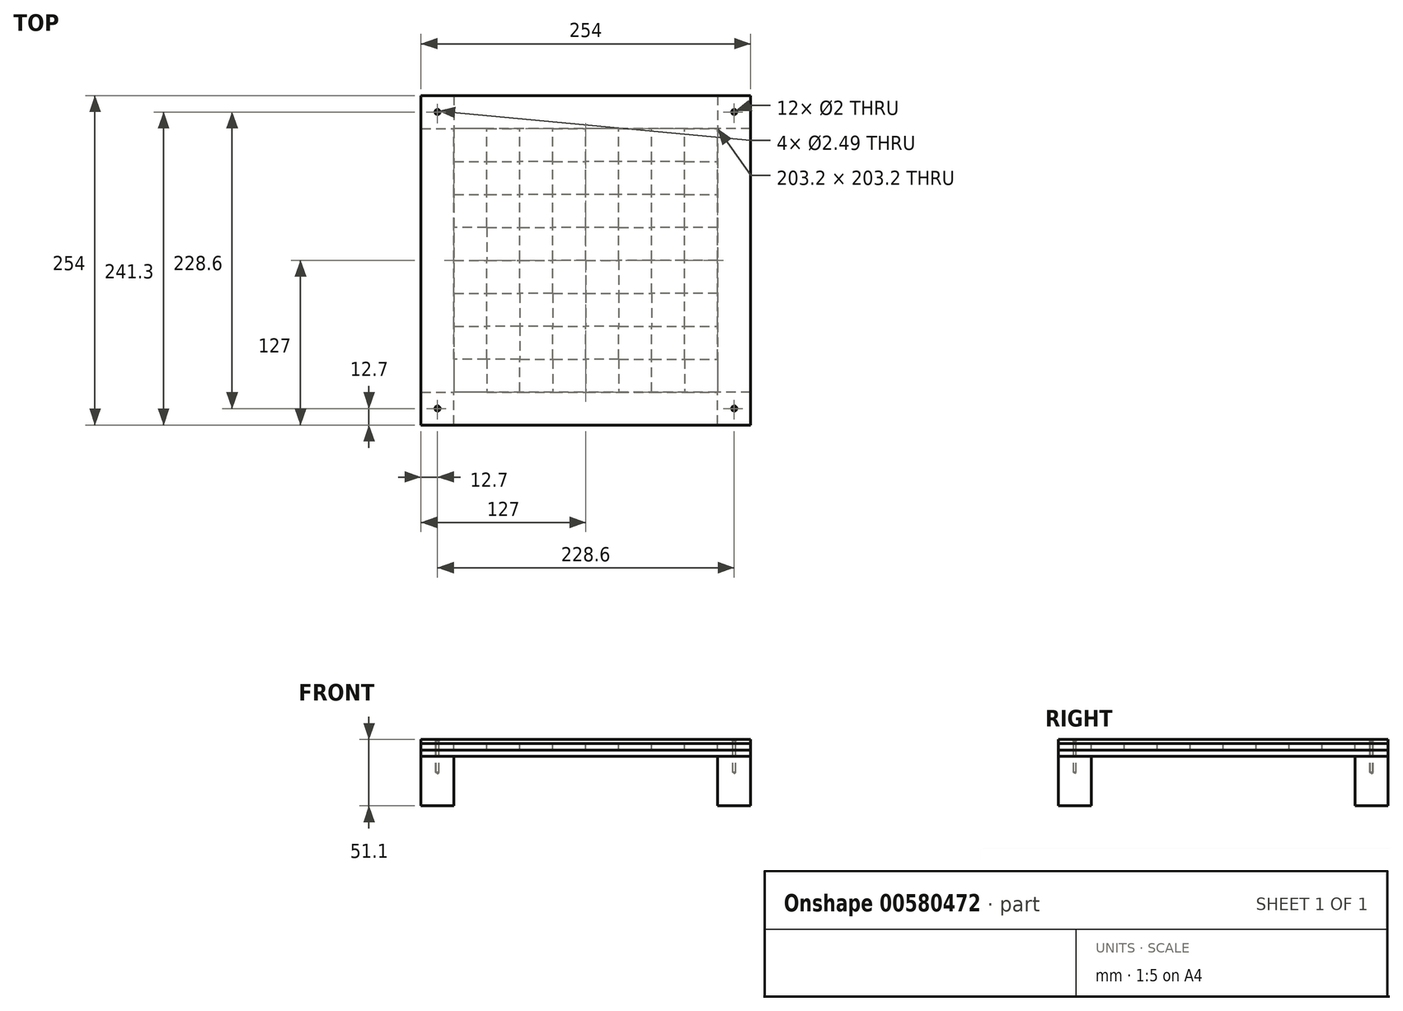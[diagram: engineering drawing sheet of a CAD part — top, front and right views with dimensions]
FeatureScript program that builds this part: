
annotation { "Feature Type Name" : "Feature", "Feature Type Description" : "" }
export const myFeature = defineFeature(function(context is Context, id is Id, definition is map)
    precondition{}
    {
        {
            var Q0;
            Q0=qCreatedBy(makeId("Top.planeOp"),FACE);
            var sketch = newSketch(context, id + "F0", { "sketchPlane" : qUnion([Q0])});
            skLineSegment(sketch, "E0.bottom", {"start": v(127, 127) * mm, "end": v(-127, 127) * mm});
            skLineSegment(sketch, "E0.top", {"start": v(127, -127) * mm, "end": v(-127, -127) * mm});
            skLineSegment(sketch, "E0.left", {"start": v(127, 127) * mm, "end": v(127, -127) * mm});
            skLineSegment(sketch, "E0.right", {"start": v(-127, 127) * mm, "end": v(-127, -127) * mm});
            skPoint(sketch, "E0.middle", {"position": v(0, 0) * mm});
            skSolve(sketch);
        }
        {
            var Q0;
            Q0=qCreatedBy(makeId("Top.planeOp"),FACE);
            var sketch = newSketch(context, id + "F1", { "sketchPlane" : qUnion([Q0])});
            skLineSegment(sketch, "E1.bottom", {"start": v(-127, 127) * mm, "end": v(127, 127) * mm});
            skLineSegment(sketch, "E1.top", {"start": v(-127, -127) * mm, "end": v(127, -127) * mm});
            skLineSegment(sketch, "E1.left", {"start": v(-127, 127) * mm, "end": v(-127, -127) * mm});
            skLineSegment(sketch, "E1.right", {"start": v(127, 127) * mm, "end": v(127, -127) * mm});
            skPoint(sketch, "E1.middle", {"position": v(0, 0) * mm});
            skSolve(sketch);
        }
        {
            var Q0;
            Q0 = qSketchRegion(id + "F1", true);
            extrude(context, id + "F2", {"entities" : qUnion([Q0]), "oppositeDirection" : true, "depth" : 5 * mm, "offsetDistance" : 25.4 * mm});
        }
        {
            var Q0;
            Q0 = qSketchRegion(id + "F0", true);
            extrude(context, id + "F3", {"entities" : qUnion([Q0]), "depth" : 3 * mm, "offsetDistance" : 25.4 * mm});
        }
        {
            var Q0;
            Q0=makeQuery(id+"F2.opExtrude","CAP_FACE",FACE,{"disambiguationData":[OSD([sQuery(id+"F1.wireOp",EDGE,"E1.bottom"),sQuery(id+"F1.wireOp",EDGE,"E1.top"),sQuery(id+"F1.wireOp",EDGE,"E1.left"),sQuery(id+"F1.wireOp",EDGE,"E1.right")])],"isStart":false});
            extrude(context, id + "F4", {"entities" : qUnion([Q0]), "depth" : 5 * mm, "offsetDistance" : 25.4 * mm});
        }
        {
            var Q0;
            Q0=makeQuery(id+"F4.opExtrude","CAP_FACE",FACE,{"disambiguationData":[OSD([sQuery(id+"F1.wireOp",EDGE,"E1.bottom"),sQuery(id+"F1.wireOp",EDGE,"E1.top"),sQuery(id+"F1.wireOp",EDGE,"E1.left"),sQuery(id+"F1.wireOp",EDGE,"E1.right")])],"isStart":false});
            var sketch = newSketch(context, id + "F5", { "sketchPlane" : qUnion([Q0])});
            skLineSegment(sketch, "E2.bottom", {"start": v(-127, 127) * mm, "end": v(-101.6, 127) * mm});
            skLineSegment(sketch, "E2.top", {"start": v(-127, 101.6) * mm, "end": v(-101.6, 101.6) * mm});
            skLineSegment(sketch, "E2.left", {"start": v(-127, 127) * mm, "end": v(-127, 101.6) * mm});
            skLineSegment(sketch, "E2.right", {"start": v(-101.6, 127) * mm, "end": v(-101.6, 101.6) * mm});
            skSolve(sketch);
        }
        {
            var Q0;
            Q0 = qSketchRegion(id + "F5", true);
            extrude(context, id + "F6", {"entities" : qUnion([Q0]), "depth" : 38.1 * mm, "offsetDistance" : 25.4 * mm});
        }
        {
            var Q0;
            Q0=makeQuery(id+"F4.opExtrude","CAP_FACE",FACE,{"disambiguationData":[OSD([sQuery(id+"F1.wireOp",EDGE,"E1.bottom"),sQuery(id+"F1.wireOp",EDGE,"E1.top"),sQuery(id+"F1.wireOp",EDGE,"E1.left"),sQuery(id+"F1.wireOp",EDGE,"E1.right")])],"isStart":false});
            var sketch = newSketch(context, id + "F7", { "sketchPlane" : qUnion([Q0])});
            skLineSegment(sketch, "E3.bottom", {"start": v(127, 127) * mm, "end": v(101.6, 127) * mm});
            skLineSegment(sketch, "E3.top", {"start": v(127, 101.6) * mm, "end": v(101.6, 101.6) * mm});
            skLineSegment(sketch, "E3.left", {"start": v(127, 127) * mm, "end": v(127, 101.6) * mm});
            skLineSegment(sketch, "E3.right", {"start": v(101.6, 127) * mm, "end": v(101.6, 101.6) * mm});
            skSolve(sketch);
        }
        {
            var Q0;
            Q0=makeQuery(id+"F7.imprint","IMPRINT",FACE,{"disambiguationData":[TD([[makeQuery(id+"F7.imprint","IMPRINT",EDGE,{"derivedFrom":sQuery(id+"F7.wireOp",EDGE,"E3.bottom")}),-1.0]])]});
            extrude(context, id + "F8", {"entities" : qUnion([Q0]), "depth" : 38.1 * mm, "offsetDistance" : 25.4 * mm});
        }
        {
            var Q0;
            Q0=makeQuery(id+"F4.opExtrude","CAP_FACE",FACE,{"disambiguationData":[OSD([sQuery(id+"F1.wireOp",EDGE,"E1.bottom"),sQuery(id+"F1.wireOp",EDGE,"E1.top"),sQuery(id+"F1.wireOp",EDGE,"E1.left"),sQuery(id+"F1.wireOp",EDGE,"E1.right")])],"isStart":false});
            var sketch = newSketch(context, id + "F9", { "sketchPlane" : qUnion([Q0])});
            skLineSegment(sketch, "E4.bottom", {"start": v(127, -127) * mm, "end": v(101.6, -127) * mm});
            skLineSegment(sketch, "E4.top", {"start": v(127, -101.6) * mm, "end": v(101.6, -101.6) * mm});
            skLineSegment(sketch, "E4.left", {"start": v(127, -127) * mm, "end": v(127, -101.6) * mm});
            skLineSegment(sketch, "E4.right", {"start": v(101.6, -127) * mm, "end": v(101.6, -101.6) * mm});
            skSolve(sketch);
        }
        {
            var Q0;
            Q0 = qSketchRegion(id + "F9", true);
            extrude(context, id + "F10", {"entities" : qUnion([Q0]), "depth" : 38.1 * mm, "offsetDistance" : 25.4 * mm});
        }
        {
            var Q0;
            Q0=makeQuery(id+"F4.opExtrude","CAP_FACE",FACE,{"disambiguationData":[OSD([sQuery(id+"F1.wireOp",EDGE,"E1.bottom"),sQuery(id+"F1.wireOp",EDGE,"E1.top"),sQuery(id+"F1.wireOp",EDGE,"E1.left"),sQuery(id+"F1.wireOp",EDGE,"E1.right")])],"isStart":false});
            var sketch = newSketch(context, id + "F11", { "sketchPlane" : qUnion([Q0])});
            skLineSegment(sketch, "E5.bottom", {"start": v(-127, -127) * mm, "end": v(-101.6, -127) * mm});
            skLineSegment(sketch, "E5.top", {"start": v(-127, -101.6) * mm, "end": v(-101.6, -101.6) * mm});
            skLineSegment(sketch, "E5.left", {"start": v(-127, -127) * mm, "end": v(-127, -101.6) * mm});
            skLineSegment(sketch, "E5.right", {"start": v(-101.6, -127) * mm, "end": v(-101.6, -101.6) * mm});
            skSolve(sketch);
        }
        {
            var Q0;
            Q0=makeQuery(id+"F11.imprint","IMPRINT",FACE,{"disambiguationData":[TD([[makeQuery(id+"F11.imprint","IMPRINT",EDGE,{"derivedFrom":sQuery(id+"F11.wireOp",EDGE,"E5.bottom")}),1.0]])]});
            extrude(context, id + "F12", {"entities" : qUnion([Q0]), "depth" : 38.1 * mm, "offsetDistance" : 25.4 * mm});
        }
        {
            var Q0;
            Q0=makeQuery(id+"F3.opExtrude","CAP_FACE",FACE,{"disambiguationData":[OSD([sQuery(id+"F0.wireOp",EDGE,"E0.bottom"),sQuery(id+"F0.wireOp",EDGE,"E0.top"),sQuery(id+"F0.wireOp",EDGE,"E0.left"),sQuery(id+"F0.wireOp",EDGE,"E0.right")])],"isStart":false});
            var sketch = newSketch(context, id + "F13", { "sketchPlane" : qUnion([Q0])});
            skCircle(sketch, "E6", {"center": v(-114.3, 114.3) * mm, "radius": 3.81 * mm});
            skSolve(sketch);
        }
        {
            var Q0;
            Q0=sQuery(id+"F13.wireOp",VERTEX,"E6.center");
            var Q1;
            Q1=makeQuery(id+"F2.opExtrude","SWEPT_BODY",BODY,{"disambiguationData":[OSD([sQuery(id+"F1.wireOp",EDGE,"E1.bottom"),sQuery(id+"F1.wireOp",EDGE,"E1.top"),sQuery(id+"F1.wireOp",EDGE,"E1.left"),sQuery(id+"F1.wireOp",EDGE,"E1.right")])]});
            var Q2;
            Q2=makeQuery(id+"F3.opExtrude","SWEPT_BODY",BODY,{"disambiguationData":[OSD([sQuery(id+"F0.wireOp",EDGE,"E0.bottom"),sQuery(id+"F0.wireOp",EDGE,"E0.top"),sQuery(id+"F0.wireOp",EDGE,"E0.left"),sQuery(id+"F0.wireOp",EDGE,"E0.right")])]});
            var Q3;
            Q3=makeQuery(id+"F4.opExtrude","SWEPT_BODY",BODY,{"disambiguationData":[OSD([sQuery(id+"F1.wireOp",EDGE,"E1.bottom"),sQuery(id+"F1.wireOp",EDGE,"E1.top"),sQuery(id+"F1.wireOp",EDGE,"E1.left"),sQuery(id+"F1.wireOp",EDGE,"E1.right")])]});
            var Q4;
            Q4=makeQuery(id+"F12.opExtrude","SWEPT_BODY",BODY,{"disambiguationData":[OSD([sQuery(id+"F11.wireOp",EDGE,"E5.bottom"),sQuery(id+"F11.wireOp",EDGE,"E5.top"),sQuery(id+"F11.wireOp",EDGE,"E5.left"),sQuery(id+"F11.wireOp",EDGE,"E5.right")])]});
            hole(context, id + "F14", {"style" : HoleStyle.SIMPLE, "endStyle" : HoleEndStyle.BLIND, "holeDiameter" : 2.5 * mm, "holeDepth" : 25.4 * mm, "isTappedThrough" : true, "tappedDepth" : 12.7 * mm, "tapClearance" : 3, "locations" : qUnion([Q0]), "scope" : qUnion([Q1, Q2, Q3, Q4])});
        }
        {
            var Q0;
            Q0=makeQuery(id+"F3.opExtrude","CAP_FACE",FACE,{"disambiguationData":[OSD([sQuery(id+"F0.wireOp",EDGE,"E0.bottom"),sQuery(id+"F0.wireOp",EDGE,"E0.top"),sQuery(id+"F0.wireOp",EDGE,"E0.left"),sQuery(id+"F0.wireOp",EDGE,"E0.right")])],"isStart":false});
            var sketch = newSketch(context, id + "F15", { "sketchPlane" : qUnion([Q0])});
            skPoint(sketch, "E7", {"position": v(-114.3, 114.3) * mm});
            skCircle(sketch, "E8", {"center": v(-114.3, 114.3) * mm, "radius": 2 * mm});
            skSolve(sketch);
        }
        {
            var Q0;
            Q0=sQuery(id+"F15.wireOp",VERTEX,"E7");
            var Q1;
            Q1=makeQuery(id+"F3.opExtrude","SWEPT_BODY",BODY,{"disambiguationData":[OSD([sQuery(id+"F0.wireOp",EDGE,"E0.bottom"),sQuery(id+"F0.wireOp",EDGE,"E0.top"),sQuery(id+"F0.wireOp",EDGE,"E0.left"),sQuery(id+"F0.wireOp",EDGE,"E0.right")])]});
            hole(context, id + "F16", {"style" : HoleStyle.C_SINK, "endStyle" : HoleEndStyle.BLIND, "holeDiameter" : 2.5 * mm, "cSinkDiameter" : 4 * mm, "cSinkAngle" : 90 * degree, "holeDepth" : 4 * mm, "isTappedThrough" : true, "tappedDepth" : 12.7 * mm, "tapClearance" : 3, "locations" : qUnion([Q0]), "scope" : qUnion([Q1])});
        }
        {
            var Q0;
            Q0=makeQuery(id+"F3.opExtrude","CAP_FACE",FACE,{"disambiguationData":[OSD([sQuery(id+"F0.wireOp",EDGE,"E0.bottom"),sQuery(id+"F0.wireOp",EDGE,"E0.top"),sQuery(id+"F0.wireOp",EDGE,"E0.left"),sQuery(id+"F0.wireOp",EDGE,"E0.right")])],"isStart":false});
            var sketch = newSketch(context, id + "F17", { "sketchPlane" : qUnion([Q0])});
            skCircle(sketch, "E9", {"center": v(114.3, 114.3) * mm, "radius": 2 * mm});
            skSolve(sketch);
        }
        {
            var Q0;
            Q0=sQuery(id+"F17.wireOp",VERTEX,"E9.center");
            var Q1;
            Q1=makeQuery(id+"F2.opExtrude","SWEPT_BODY",BODY,{"disambiguationData":[OSD([sQuery(id+"F1.wireOp",EDGE,"E1.bottom"),sQuery(id+"F1.wireOp",EDGE,"E1.top"),sQuery(id+"F1.wireOp",EDGE,"E1.left"),sQuery(id+"F1.wireOp",EDGE,"E1.right")])]});
            var Q2;
            Q2=makeQuery(id+"F3.opExtrude","SWEPT_BODY",BODY,{"disambiguationData":[OSD([sQuery(id+"F0.wireOp",EDGE,"E0.bottom"),sQuery(id+"F0.wireOp",EDGE,"E0.top"),sQuery(id+"F0.wireOp",EDGE,"E0.left"),sQuery(id+"F0.wireOp",EDGE,"E0.right")])]});
            var Q3;
            Q3=makeQuery(id+"F4.opExtrude","SWEPT_BODY",BODY,{"disambiguationData":[OSD([sQuery(id+"F1.wireOp",EDGE,"E1.bottom"),sQuery(id+"F1.wireOp",EDGE,"E1.top"),sQuery(id+"F1.wireOp",EDGE,"E1.left"),sQuery(id+"F1.wireOp",EDGE,"E1.right")])]});
            var Q4;
            Q4=makeQuery(id+"F10.opExtrude","SWEPT_BODY",BODY,{"disambiguationData":[OSD([sQuery(id+"F9.wireOp",EDGE,"E4.bottom"),sQuery(id+"F9.wireOp",EDGE,"E4.top"),sQuery(id+"F9.wireOp",EDGE,"E4.left"),sQuery(id+"F9.wireOp",EDGE,"E4.right")])]});
            hole(context, id + "F18", {"style" : HoleStyle.SIMPLE, "endStyle" : HoleEndStyle.BLIND, "holeDiameter" : 2 * mm, "holeDepth" : 25.4 * mm, "isTappedThrough" : true, "tappedDepth" : 12.7 * mm, "tapClearance" : 3, "locations" : qUnion([Q0]), "scope" : qUnion([Q1, Q2, Q3, Q4])});
        }
        {
            var Q0;
            Q0=makeQuery(id+"F3.opExtrude","CAP_FACE",FACE,{"disambiguationData":[OSD([sQuery(id+"F0.wireOp",EDGE,"E0.bottom"),sQuery(id+"F0.wireOp",EDGE,"E0.top"),sQuery(id+"F0.wireOp",EDGE,"E0.left"),sQuery(id+"F0.wireOp",EDGE,"E0.right")])],"isStart":false});
            var sketch = newSketch(context, id + "F19", { "sketchPlane" : qUnion([Q0])});
            skPoint(sketch, "E10", {"position": v(114.3, 114.3) * mm});
            skSolve(sketch);
        }
        {
            var Q0;
            Q0=sQuery(id+"F19.wireOp",VERTEX,"E10");
            var Q1;
            Q1=makeQuery(id+"F3.opExtrude","SWEPT_BODY",BODY,{"disambiguationData":[OSD([sQuery(id+"F0.wireOp",EDGE,"E0.bottom"),sQuery(id+"F0.wireOp",EDGE,"E0.top"),sQuery(id+"F0.wireOp",EDGE,"E0.left"),sQuery(id+"F0.wireOp",EDGE,"E0.right")])]});
            hole(context, id + "F20", {"style" : HoleStyle.C_SINK, "endStyle" : HoleEndStyle.BLIND, "holeDiameter" : 2 * mm, "cSinkDiameter" : 4 * mm, "cSinkAngle" : 90 * degree, "holeDepth" : 4 * mm, "isTappedThrough" : true, "tappedDepth" : 12.7 * mm, "tapClearance" : 3, "startFromSketch" : true, "locations" : qUnion([Q0]), "scope" : qUnion([Q1])});
        }
        {
            var Q0;
            Q0=makeQuery(id+"F3.opExtrude","CAP_FACE",FACE,{"disambiguationData":[OSD([sQuery(id+"F0.wireOp",EDGE,"E0.bottom"),sQuery(id+"F0.wireOp",EDGE,"E0.top"),sQuery(id+"F0.wireOp",EDGE,"E0.left"),sQuery(id+"F0.wireOp",EDGE,"E0.right")])],"isStart":false});
            var sketch = newSketch(context, id + "F21", { "sketchPlane" : qUnion([Q0])});
            skCircle(sketch, "E11", {"center": v(114.3, -114.3) * mm, "radius": 1 * mm});
            skCircle(sketch, "E12", {"center": v(-114.3, -114.3) * mm, "radius": 1 * mm});
            skSolve(sketch);
        }
        {
            var Q0;
            Q0=sQuery(id+"F21.wireOp",VERTEX,"E12.center");
            var Q1;
            Q1=makeQuery(id+"F2.opExtrude","SWEPT_BODY",BODY,{"disambiguationData":[OSD([sQuery(id+"F1.wireOp",EDGE,"E1.bottom"),sQuery(id+"F1.wireOp",EDGE,"E1.top"),sQuery(id+"F1.wireOp",EDGE,"E1.left"),sQuery(id+"F1.wireOp",EDGE,"E1.right")])]});
            var Q2;
            Q2=makeQuery(id+"F3.opExtrude","SWEPT_BODY",BODY,{"disambiguationData":[OSD([sQuery(id+"F0.wireOp",EDGE,"E0.bottom"),sQuery(id+"F0.wireOp",EDGE,"E0.top"),sQuery(id+"F0.wireOp",EDGE,"E0.left"),sQuery(id+"F0.wireOp",EDGE,"E0.right")])]});
            var Q3;
            Q3=makeQuery(id+"F4.opExtrude","SWEPT_BODY",BODY,{"disambiguationData":[OSD([sQuery(id+"F1.wireOp",EDGE,"E1.bottom"),sQuery(id+"F1.wireOp",EDGE,"E1.top"),sQuery(id+"F1.wireOp",EDGE,"E1.left"),sQuery(id+"F1.wireOp",EDGE,"E1.right")])]});
            var Q4;
            Q4=makeQuery(id+"F6.opExtrude","SWEPT_BODY",BODY,{"disambiguationData":[OSD([sQuery(id+"F5.wireOp",EDGE,"E2.bottom"),sQuery(id+"F5.wireOp",EDGE,"E2.top"),sQuery(id+"F5.wireOp",EDGE,"E2.left"),sQuery(id+"F5.wireOp",EDGE,"E2.right")])]});
            hole(context, id + "F22", {"style" : HoleStyle.SIMPLE, "endStyle" : HoleEndStyle.BLIND, "holeDiameter" : 2 * mm, "holeDepth" : 25.4 * mm, "isTappedThrough" : true, "tappedDepth" : 12 * mm, "tapClearance" : 3, "locations" : qUnion([Q0]), "scope" : qUnion([Q1, Q2, Q3, Q4])});
        }
        {
            var Q0;
            Q0=sQuery(id+"F21.wireOp",VERTEX,"E11.center");
            var Q1;
            Q1=makeQuery(id+"F2.opExtrude","SWEPT_BODY",BODY,{"disambiguationData":[OSD([sQuery(id+"F1.wireOp",EDGE,"E1.bottom"),sQuery(id+"F1.wireOp",EDGE,"E1.top"),sQuery(id+"F1.wireOp",EDGE,"E1.left"),sQuery(id+"F1.wireOp",EDGE,"E1.right")])]});
            var Q2;
            Q2=makeQuery(id+"F3.opExtrude","SWEPT_BODY",BODY,{"disambiguationData":[OSD([sQuery(id+"F0.wireOp",EDGE,"E0.bottom"),sQuery(id+"F0.wireOp",EDGE,"E0.top"),sQuery(id+"F0.wireOp",EDGE,"E0.left"),sQuery(id+"F0.wireOp",EDGE,"E0.right")])]});
            var Q3;
            Q3=makeQuery(id+"F4.opExtrude","SWEPT_BODY",BODY,{"disambiguationData":[OSD([sQuery(id+"F1.wireOp",EDGE,"E1.bottom"),sQuery(id+"F1.wireOp",EDGE,"E1.top"),sQuery(id+"F1.wireOp",EDGE,"E1.left"),sQuery(id+"F1.wireOp",EDGE,"E1.right")])]});
            var Q4;
            Q4=makeQuery(id+"F8.opExtrude","SWEPT_BODY",BODY,{"disambiguationData":[OSD([sQuery(id+"F7.wireOp",EDGE,"E3.bottom"),sQuery(id+"F7.wireOp",EDGE,"E3.top"),sQuery(id+"F7.wireOp",EDGE,"E3.left"),sQuery(id+"F7.wireOp",EDGE,"E3.right")])]});
            hole(context, id + "F23", {"style" : HoleStyle.SIMPLE, "endStyle" : HoleEndStyle.BLIND, "holeDiameter" : 2 * mm, "holeDepth" : 25.4 * mm, "isTappedThrough" : true, "tappedDepth" : 12 * mm, "tapClearance" : 3, "locations" : qUnion([Q0]), "scope" : qUnion([Q1, Q2, Q3, Q4])});
        }
        {
            var Q0;
            Q0=sQuery(id+"F21.wireOp",VERTEX,"E11.center");
            var Q1;
            Q1=makeQuery(id+"F3.opExtrude","SWEPT_BODY",BODY,{"disambiguationData":[OSD([sQuery(id+"F0.wireOp",EDGE,"E0.bottom"),sQuery(id+"F0.wireOp",EDGE,"E0.top"),sQuery(id+"F0.wireOp",EDGE,"E0.left"),sQuery(id+"F0.wireOp",EDGE,"E0.right")])]});
            hole(context, id + "F24", {"style" : HoleStyle.C_SINK, "endStyle" : HoleEndStyle.BLIND, "holeDiameter" : 2 * mm, "cSinkDiameter" : 4 * mm, "cSinkAngle" : 90 * degree, "holeDepth" : 4 * mm, "isTappedThrough" : true, "tappedDepth" : 12 * mm, "tapClearance" : 3, "locations" : qUnion([Q0]), "scope" : qUnion([Q1])});
        }
        {
            var Q0;
            Q0=sQuery(id+"F21.wireOp",VERTEX,"E12.center");
            var Q1;
            Q1=makeQuery(id+"F3.opExtrude","SWEPT_BODY",BODY,{"disambiguationData":[OSD([sQuery(id+"F0.wireOp",EDGE,"E0.bottom"),sQuery(id+"F0.wireOp",EDGE,"E0.top"),sQuery(id+"F0.wireOp",EDGE,"E0.left"),sQuery(id+"F0.wireOp",EDGE,"E0.right")])]});
            hole(context, id + "F25", {"style" : HoleStyle.C_SINK, "endStyle" : HoleEndStyle.BLIND, "holeDiameter" : 2 * mm, "cSinkDiameter" : 4 * mm, "cSinkAngle" : 90 * degree, "holeDepth" : 4 * mm, "isTappedThrough" : true, "tappedDepth" : 12 * mm, "tapClearance" : 3, "locations" : qUnion([Q0]), "scope" : qUnion([Q1])});
        }
        {
            var Q0;
            Q0=makeQuery(id+"F0.imprint","IMPRINT",FACE,{"disambiguationData":[TD([[makeQuery(id+"F0.imprint","IMPRINT",EDGE,{"derivedFrom":sQuery(id+"F0.wireOp",EDGE,"E0.bottom")}),1.0]])]});
            var sketch = newSketch(context, id + "F26", { "sketchPlane" : qUnion([Q0])});
            skLineSegment(sketch, "E13.bottom", {"start": v(101.6, 101.6) * mm, "end": v(-101.6, 101.6) * mm});
            skLineSegment(sketch, "E13.top", {"start": v(101.6, -101.6) * mm, "end": v(-101.6, -101.6) * mm});
            skLineSegment(sketch, "E13.left", {"start": v(101.6, 101.6) * mm, "end": v(101.6, -101.6) * mm});
            skLineSegment(sketch, "E13.right", {"start": v(-101.6, 101.6) * mm, "end": v(-101.6, -101.6) * mm});
            skPoint(sketch, "E13.middle", {"position": v(0, 0) * mm});
            skSolve(sketch);
        }
        {
            var Q0;
            Q0=makeQuery(id+"F26.imprint","IMPRINT",FACE,{"disambiguationData":[TD([[makeQuery(id+"F26.imprint","IMPRINT",EDGE,{"derivedFrom":sQuery(id+"F26.wireOp",EDGE,"E13.bottom")}),1.0]])]});
            extrude(context, id + "F27", {"entities" : qUnion([Q0]), "operationType" : NewBodyOperationType.REMOVE, "oppositeDirection" : true, "depth" : 5 * mm, "offsetDistance" : 25 * mm});
        }
        {
            var Q0;
            Q0=makeQuery(id+"F26.imprint","IMPRINT",FACE,{"disambiguationData":[TD([[makeQuery(id+"F26.imprint","IMPRINT",EDGE,{"derivedFrom":sQuery(id+"F26.wireOp",EDGE,"E13.bottom")}),1.0]])]});
            var sketch = newSketch(context, id + "F28", { "sketchPlane" : qUnion([Q0])});
            skLineSegment(sketch, "E14.bottom", {"start": v(0, 0) * mm, "end": v(-25.4, 0) * mm});
            skLineSegment(sketch, "E14.top", {"start": v(0, -25.4) * mm, "end": v(-25.4, -25.4) * mm});
            skLineSegment(sketch, "E14.left", {"start": v(0, 0) * mm, "end": v(0, -25.4) * mm});
            skLineSegment(sketch, "E14.right", {"start": v(-25.4, 0) * mm, "end": v(-25.4, -25.4) * mm});
            skSolve(sketch);
        }
        {
            var Q0;
            Q0=makeQuery(id+"F28.imprint","IMPRINT",FACE,{"disambiguationData":[TD([[makeQuery(id+"F28.imprint","IMPRINT",EDGE,{"derivedFrom":sQuery(id+"F28.wireOp",EDGE,"E14.bottom")}),1.0]])]});
            var Q1;
            Q1=sQuery(id+"F28.wireOp",EDGE,"E14.top");
            var Q2;
            Q2=sQuery(id+"F28.wireOp",EDGE,"E14.left");
            var Q3;
            Q3=sQuery(id+"F28.wireOp",EDGE,"E14.right");
            var Q4;
            Q4=sQuery(id+"F28.wireOp",EDGE,"E14.bottom");
            extrude(context, id + "F29", {"entities" : qUnion([Q0]), "surfaceEntities" : qUnion([Q1, Q2, Q3, Q4]), "oppositeDirection" : true, "depth" : 5 * mm, "offsetDistance" : 25 * mm});
        }
        {
            var Q0;
            Q0=makeQuery(id+"F26.imprint","IMPRINT",FACE,{"disambiguationData":[TD([[makeQuery(id+"F26.imprint","IMPRINT",EDGE,{"derivedFrom":sQuery(id+"F26.wireOp",EDGE,"E13.bottom")}),1.0]])]});
            var sketch = newSketch(context, id + "F30", { "sketchPlane" : qUnion([Q0])});
            skLineSegment(sketch, "E15.bottom", {"start": v(0, 0) * mm, "end": v(-25.4, 0) * mm});
            skLineSegment(sketch, "E15.top", {"start": v(0, 25.4) * mm, "end": v(-25.4, 25.4) * mm});
            skLineSegment(sketch, "E15.left", {"start": v(0, 0) * mm, "end": v(0, 25.4) * mm});
            skLineSegment(sketch, "E15.right", {"start": v(-25.4, 0) * mm, "end": v(-25.4, 25.4) * mm});
            skSolve(sketch);
        }
        {
            var Q0;
            Q0 = qSketchRegion(id + "F30", true);
            extrude(context, id + "F31", {"entities" : qUnion([Q0]), "oppositeDirection" : true, "depth" : 5 * mm, "offsetDistance" : 25 * mm});
        }
        {
            var Q0;
            Q0=makeQuery(id+"F0.imprint","IMPRINT",FACE,{"disambiguationData":[TD([[makeQuery(id+"F0.imprint","IMPRINT",EDGE,{"derivedFrom":sQuery(id+"F0.wireOp",EDGE,"E0.bottom")}),1.0]])]});
            var sketch = newSketch(context, id + "F32", { "sketchPlane" : qUnion([Q0])});
            skLineSegment(sketch, "E16.bottom", {"start": v(0, 0) * mm, "end": v(25.4, 0) * mm});
            skLineSegment(sketch, "E16.top", {"start": v(0, -25.4) * mm, "end": v(25.4, -25.4) * mm});
            skLineSegment(sketch, "E16.left", {"start": v(0, 0) * mm, "end": v(0, -25.4) * mm});
            skLineSegment(sketch, "E16.right", {"start": v(25.4, 0) * mm, "end": v(25.4, -25.4) * mm});
            skSolve(sketch);
        }
        {
            var Q0;
            Q0=makeQuery(id+"F32.imprint","IMPRINT",FACE,{"disambiguationData":[TD([[makeQuery(id+"F32.imprint","IMPRINT",EDGE,{"derivedFrom":sQuery(id+"F32.wireOp",EDGE,"E16.bottom")}),-1.0]])]});
            var Q1;
            Q1=sQuery(id+"F32.wireOp",EDGE,"E16.left");
            var Q2;
            Q2=sQuery(id+"F32.wireOp",EDGE,"E16.right");
            var Q3;
            Q3=sQuery(id+"F32.wireOp",EDGE,"E16.bottom");
            var Q4;
            Q4=sQuery(id+"F32.wireOp",EDGE,"E16.top");
            extrude(context, id + "F33", {"entities" : qUnion([Q0]), "surfaceEntities" : qUnion([Q1, Q2, Q3, Q4]), "oppositeDirection" : true, "depth" : 5 * mm, "offsetDistance" : 25 * mm});
        }
        {
            var Q0;
            Q0=makeQuery(id+"F0.imprint","IMPRINT",FACE,{"disambiguationData":[TD([[makeQuery(id+"F0.imprint","IMPRINT",EDGE,{"derivedFrom":sQuery(id+"F0.wireOp",EDGE,"E0.bottom")}),1.0]])]});
            var sketch = newSketch(context, id + "F34", { "sketchPlane" : qUnion([Q0])});
            skLineSegment(sketch, "E17.bottom", {"start": v(25.4, -25.4) * mm, "end": v(50.8, -25.4) * mm});
            skLineSegment(sketch, "E17.top", {"start": v(25.4, -50.8) * mm, "end": v(50.8, -50.8) * mm});
            skLineSegment(sketch, "E17.left", {"start": v(25.4, -25.4) * mm, "end": v(25.4, -50.8) * mm});
            skLineSegment(sketch, "E17.right", {"start": v(50.8, -25.4) * mm, "end": v(50.8, -50.8) * mm});
            skSolve(sketch);
        }
        {
            var Q0;
            Q0=makeQuery(id+"F34.imprint","IMPRINT",FACE,{"disambiguationData":[TD([[makeQuery(id+"F34.imprint","IMPRINT",EDGE,{"derivedFrom":sQuery(id+"F34.wireOp",EDGE,"E17.bottom")}),-1.0]])]});
            var Q1;
            Q1=sQuery(id+"F34.wireOp",EDGE,"E17.bottom");
            var Q2;
            Q2=sQuery(id+"F34.wireOp",EDGE,"E17.top");
            var Q3;
            Q3=sQuery(id+"F34.wireOp",EDGE,"E17.left");
            var Q4;
            Q4=sQuery(id+"F34.wireOp",EDGE,"E17.right");
            extrude(context, id + "F35", {"entities" : qUnion([Q0]), "surfaceEntities" : qUnion([Q1, Q2, Q3, Q4]), "oppositeDirection" : true, "depth" : 5 * mm, "offsetDistance" : 25 * mm});
        }
        {
            var Q0;
            Q0=makeQuery(id+"F0.imprint","IMPRINT",FACE,{"disambiguationData":[TD([[makeQuery(id+"F0.imprint","IMPRINT",EDGE,{"derivedFrom":sQuery(id+"F0.wireOp",EDGE,"E0.bottom")}),1.0]])]});
            var sketch = newSketch(context, id + "F36", { "sketchPlane" : qUnion([Q0])});
            skLineSegment(sketch, "E18.bottom", {"start": v(0, 0) * mm, "end": v(25.4, 0) * mm});
            skLineSegment(sketch, "E18.top", {"start": v(0, 25.4) * mm, "end": v(25.4, 25.4) * mm});
            skLineSegment(sketch, "E18.left", {"start": v(0, 0) * mm, "end": v(0, 25.4) * mm});
            skLineSegment(sketch, "E18.right", {"start": v(25.4, 0) * mm, "end": v(25.4, 25.4) * mm});
            skSolve(sketch);
        }
        {
            var Q0;
            Q0=makeQuery(id+"F36.imprint","IMPRINT",FACE,{"disambiguationData":[TD([[makeQuery(id+"F36.imprint","IMPRINT",EDGE,{"derivedFrom":sQuery(id+"F36.wireOp",EDGE,"E18.bottom")}),1.0]])]});
            var Q1;
            Q1=sQuery(id+"F36.wireOp",EDGE,"E18.bottom");
            var Q2;
            Q2=sQuery(id+"F36.wireOp",EDGE,"E18.left");
            var Q3;
            Q3=sQuery(id+"F36.wireOp",EDGE,"E18.top");
            var Q4;
            Q4=sQuery(id+"F36.wireOp",EDGE,"E18.right");
            extrude(context, id + "F37", {"entities" : qUnion([Q0]), "surfaceEntities" : qUnion([Q1, Q2, Q3, Q4]), "oppositeDirection" : true, "depth" : 5 * mm, "offsetDistance" : 25 * mm});
        }
        {
            var Q0;
            Q0=makeQuery(id+"F37.opExtrude","SWEPT_BODY",BODY,{"disambiguationData":[OSD([sQuery(id+"F36.wireOp",EDGE,"E18.bottom"),sQuery(id+"F36.wireOp",EDGE,"E18.top"),sQuery(id+"F36.wireOp",EDGE,"E18.left"),sQuery(id+"F36.wireOp",EDGE,"E18.right")])]});
            transform(context, id + "F38", {"entities" : qUnion([Q0]), "transformType" : TransformType.TRANSLATION_3D, "dx" : 25.4 * mm, "dy" : 25.4 * mm, "dz" : 0 * mm, "makeCopy" : true});
        }
        {
            var Q0;
            Q0=makeQuery(id+"F38.opPattern","COPY",BODY,{"derivedFrom":makeQuery(id+"F37.opExtrude","SWEPT_BODY",BODY,{"disambiguationData":[OSD([sQuery(id+"F36.wireOp",EDGE,"E18.bottom"),sQuery(id+"F36.wireOp",EDGE,"E18.top"),sQuery(id+"F36.wireOp",EDGE,"E18.left"),sQuery(id+"F36.wireOp",EDGE,"E18.right")])]}),"instanceName":"1"});
            transform(context, id + "F39", {"entities" : qUnion([Q0]), "transformType" : TransformType.TRANSLATION_3D, "dx" : 25.4 * mm, "dy" : 25.4 * mm, "dz" : 0 * mm, "makeCopy" : true});
        }
        {
            var Q0;
            Q0=makeQuery(id+"F39.opPattern","COPY",BODY,{"derivedFrom":makeQuery(id+"F38.opPattern","COPY",BODY,{"derivedFrom":makeQuery(id+"F37.opExtrude","SWEPT_BODY",BODY,{"disambiguationData":[OSD([sQuery(id+"F36.wireOp",EDGE,"E18.bottom"),sQuery(id+"F36.wireOp",EDGE,"E18.top"),sQuery(id+"F36.wireOp",EDGE,"E18.left"),sQuery(id+"F36.wireOp",EDGE,"E18.right")])]}),"instanceName":"1"}),"instanceName":"1"});
            transform(context, id + "F40", {"entities" : qUnion([Q0]), "transformType" : TransformType.TRANSLATION_3D, "dx" : 25.4 * mm, "dy" : 25.4 * mm, "dz" : 0 * mm, "makeCopy" : true});
        }
        {
            var Q0;
            Q0=makeQuery(id+"F29.opExtrude","SWEPT_BODY",BODY,{"disambiguationData":[OSD([sQuery(id+"F28.wireOp",EDGE,"E14.bottom"),sQuery(id+"F28.wireOp",EDGE,"E14.top"),sQuery(id+"F28.wireOp",EDGE,"E14.left"),sQuery(id+"F28.wireOp",EDGE,"E14.right")])]});
            transform(context, id + "F41", {"entities" : qUnion([Q0]), "transformType" : TransformType.TRANSLATION_3D, "dx" : -25.4 * mm, "dy" : -25.4 * mm, "dz" : 0 * mm, "makeCopy" : true});
        }
        {
            var Q0;
            Q0=makeQuery(id+"F41.opPattern","COPY",BODY,{"derivedFrom":makeQuery(id+"F29.opExtrude","SWEPT_BODY",BODY,{"disambiguationData":[OSD([sQuery(id+"F28.wireOp",EDGE,"E14.bottom"),sQuery(id+"F28.wireOp",EDGE,"E14.top"),sQuery(id+"F28.wireOp",EDGE,"E14.left"),sQuery(id+"F28.wireOp",EDGE,"E14.right")])]}),"instanceName":"1"});
            transform(context, id + "F42", {"entities" : qUnion([Q0]), "transformType" : TransformType.TRANSLATION_3D, "dx" : -25.4 * mm, "dy" : -25.4 * mm, "dz" : 0 * mm, "makeCopy" : true});
        }
        {
            var Q0;
            Q0=makeQuery(id+"F42.opPattern","COPY",BODY,{"derivedFrom":makeQuery(id+"F41.opPattern","COPY",BODY,{"derivedFrom":makeQuery(id+"F29.opExtrude","SWEPT_BODY",BODY,{"disambiguationData":[OSD([sQuery(id+"F28.wireOp",EDGE,"E14.bottom"),sQuery(id+"F28.wireOp",EDGE,"E14.top"),sQuery(id+"F28.wireOp",EDGE,"E14.left"),sQuery(id+"F28.wireOp",EDGE,"E14.right")])]}),"instanceName":"1"}),"instanceName":"1"});
            transform(context, id + "F43", {"entities" : qUnion([Q0]), "transformType" : TransformType.TRANSLATION_3D, "dx" : -25.4 * mm, "dy" : -25.4 * mm, "dz" : 0 * mm, "makeCopy" : true});
        }
        {
            var Q0;
            Q0=makeQuery(id+"F31.opExtrude","SWEPT_BODY",BODY,{"disambiguationData":[OSD([sQuery(id+"F30.wireOp",EDGE,"E15.bottom"),sQuery(id+"F30.wireOp",EDGE,"E15.top"),sQuery(id+"F30.wireOp",EDGE,"E15.left"),sQuery(id+"F30.wireOp",EDGE,"E15.right")])]});
            transform(context, id + "F44", {"entities" : qUnion([Q0]), "transformType" : TransformType.TRANSLATION_3D, "dx" : -25.4 * mm, "dy" : 25.4 * mm, "dz" : 0 * mm, "makeCopy" : true});
        }
        {
            var Q0;
            Q0=makeQuery(id+"F44.opPattern","COPY",BODY,{"derivedFrom":makeQuery(id+"F31.opExtrude","SWEPT_BODY",BODY,{"disambiguationData":[OSD([sQuery(id+"F30.wireOp",EDGE,"E15.bottom"),sQuery(id+"F30.wireOp",EDGE,"E15.top"),sQuery(id+"F30.wireOp",EDGE,"E15.left"),sQuery(id+"F30.wireOp",EDGE,"E15.right")])]}),"instanceName":"1"});
            transform(context, id + "F45", {"entities" : qUnion([Q0]), "transformType" : TransformType.TRANSLATION_3D, "dx" : -25.4 * mm, "dy" : 25.4 * mm, "dz" : 0 * mm, "makeCopy" : true});
        }
        {
            var Q0;
            Q0=makeQuery(id+"F45.opPattern","COPY",BODY,{"derivedFrom":makeQuery(id+"F44.opPattern","COPY",BODY,{"derivedFrom":makeQuery(id+"F31.opExtrude","SWEPT_BODY",BODY,{"disambiguationData":[OSD([sQuery(id+"F30.wireOp",EDGE,"E15.bottom"),sQuery(id+"F30.wireOp",EDGE,"E15.top"),sQuery(id+"F30.wireOp",EDGE,"E15.left"),sQuery(id+"F30.wireOp",EDGE,"E15.right")])]}),"instanceName":"1"}),"instanceName":"1"});
            transform(context, id + "F46", {"entities" : qUnion([Q0]), "transformType" : TransformType.TRANSLATION_3D, "dx" : -25.4 * mm, "dy" : 25.4 * mm, "dz" : 0 * mm, "makeCopy" : true});
        }
        {
            var Q0;
            Q0=makeQuery(id+"F35.opExtrude","SWEPT_BODY",BODY,{"disambiguationData":[OSD([sQuery(id+"F34.wireOp",EDGE,"E17.bottom"),sQuery(id+"F34.wireOp",EDGE,"E17.top"),sQuery(id+"F34.wireOp",EDGE,"E17.left"),sQuery(id+"F34.wireOp",EDGE,"E17.right")])]});
            transform(context, id + "F47", {"entities" : qUnion([Q0]), "transformType" : TransformType.TRANSLATION_3D, "dx" : 25.4 * mm, "dy" : -25.4 * mm, "dz" : 0 * mm, "makeCopy" : true});
        }
        {
            var Q0;
            Q0=makeQuery(id+"F47.opPattern","COPY",BODY,{"derivedFrom":makeQuery(id+"F35.opExtrude","SWEPT_BODY",BODY,{"disambiguationData":[OSD([sQuery(id+"F34.wireOp",EDGE,"E17.bottom"),sQuery(id+"F34.wireOp",EDGE,"E17.top"),sQuery(id+"F34.wireOp",EDGE,"E17.left"),sQuery(id+"F34.wireOp",EDGE,"E17.right")])]}),"instanceName":"1"});
            transform(context, id + "F48", {"entities" : qUnion([Q0]), "transformType" : TransformType.TRANSLATION_3D, "dx" : 25.4 * mm, "dy" : -25.4 * mm, "dz" : 0 * mm, "makeCopy" : true});
        }
        {
            var Q0;
            Q0=makeQuery(id+"F48.opPattern","COPY",BODY,{"derivedFrom":makeQuery(id+"F47.opPattern","COPY",BODY,{"derivedFrom":makeQuery(id+"F35.opExtrude","SWEPT_BODY",BODY,{"disambiguationData":[OSD([sQuery(id+"F34.wireOp",EDGE,"E17.bottom"),sQuery(id+"F34.wireOp",EDGE,"E17.top"),sQuery(id+"F34.wireOp",EDGE,"E17.left"),sQuery(id+"F34.wireOp",EDGE,"E17.right")])]}),"instanceName":"1"}),"instanceName":"1"});
            transform(context, id + "F49", {"entities" : qUnion([Q0]), "transformType" : TransformType.TRANSLATION_3D, "dx" : -50.8 * mm, "dy" : 0 * mm, "dz" : 0 * mm, "makeCopy" : true});
        }
        {
            var Q0;
            Q0=makeQuery(id+"F49.opPattern","COPY",BODY,{"derivedFrom":makeQuery(id+"F48.opPattern","COPY",BODY,{"derivedFrom":makeQuery(id+"F47.opPattern","COPY",BODY,{"derivedFrom":makeQuery(id+"F35.opExtrude","SWEPT_BODY",BODY,{"disambiguationData":[OSD([sQuery(id+"F34.wireOp",EDGE,"E17.bottom"),sQuery(id+"F34.wireOp",EDGE,"E17.top"),sQuery(id+"F34.wireOp",EDGE,"E17.left"),sQuery(id+"F34.wireOp",EDGE,"E17.right")])]}),"instanceName":"1"}),"instanceName":"1"}),"instanceName":"1"});
            transform(context, id + "F50", {"entities" : qUnion([Q0]), "transformType" : TransformType.TRANSLATION_3D, "dx" : -50.8 * mm, "dy" : 0 * mm, "dz" : 0 * mm, "makeCopy" : true});
        }
        {
            var Q0;
            Q0=makeQuery(id+"F50.opPattern","COPY",BODY,{"derivedFrom":makeQuery(id+"F49.opPattern","COPY",BODY,{"derivedFrom":makeQuery(id+"F48.opPattern","COPY",BODY,{"derivedFrom":makeQuery(id+"F47.opPattern","COPY",BODY,{"derivedFrom":makeQuery(id+"F35.opExtrude","SWEPT_BODY",BODY,{"disambiguationData":[OSD([sQuery(id+"F34.wireOp",EDGE,"E17.bottom"),sQuery(id+"F34.wireOp",EDGE,"E17.top"),sQuery(id+"F34.wireOp",EDGE,"E17.left"),sQuery(id+"F34.wireOp",EDGE,"E17.right")])]}),"instanceName":"1"}),"instanceName":"1"}),"instanceName":"1"}),"instanceName":"1"});
            transform(context, id + "F51", {"entities" : qUnion([Q0]), "transformType" : TransformType.TRANSLATION_3D, "dx" : -50.8 * mm, "dy" : 0 * mm, "dz" : 0 * mm, "makeCopy" : true});
        }
        {
            var Q0;
            Q0=makeQuery(id+"F51.opPattern","COPY",BODY,{"derivedFrom":makeQuery(id+"F50.opPattern","COPY",BODY,{"derivedFrom":makeQuery(id+"F49.opPattern","COPY",BODY,{"derivedFrom":makeQuery(id+"F48.opPattern","COPY",BODY,{"derivedFrom":makeQuery(id+"F47.opPattern","COPY",BODY,{"derivedFrom":makeQuery(id+"F35.opExtrude","SWEPT_BODY",BODY,{"disambiguationData":[OSD([sQuery(id+"F34.wireOp",EDGE,"E17.bottom"),sQuery(id+"F34.wireOp",EDGE,"E17.top"),sQuery(id+"F34.wireOp",EDGE,"E17.left"),sQuery(id+"F34.wireOp",EDGE,"E17.right")])]}),"instanceName":"1"}),"instanceName":"1"}),"instanceName":"1"}),"instanceName":"1"}),"instanceName":"1"});
            transform(context, id + "F52", {"entities" : qUnion([Q0]), "transformType" : TransformType.TRANSLATION_3D, "dx" : 0 * mm, "dy" : 50.8 * mm, "dz" : 0 * mm, "makeCopy" : true});
        }
        {
            var Q0;
            Q0=makeQuery(id+"F51.opPattern","COPY",BODY,{"derivedFrom":makeQuery(id+"F50.opPattern","COPY",BODY,{"derivedFrom":makeQuery(id+"F49.opPattern","COPY",BODY,{"derivedFrom":makeQuery(id+"F48.opPattern","COPY",BODY,{"derivedFrom":makeQuery(id+"F47.opPattern","COPY",BODY,{"derivedFrom":makeQuery(id+"F35.opExtrude","SWEPT_BODY",BODY,{"disambiguationData":[OSD([sQuery(id+"F34.wireOp",EDGE,"E17.bottom"),sQuery(id+"F34.wireOp",EDGE,"E17.top"),sQuery(id+"F34.wireOp",EDGE,"E17.left"),sQuery(id+"F34.wireOp",EDGE,"E17.right")])]}),"instanceName":"1"}),"instanceName":"1"}),"instanceName":"1"}),"instanceName":"1"}),"instanceName":"1"});
            transform(context, id + "F53", {"entities" : qUnion([Q0]), "transformType" : TransformType.TRANSLATION_3D, "dx" : 0 * mm, "dy" : 50.8 * mm, "dz" : 0 * mm, "makeCopy" : true});
        }
        {
            var Q0;
            Q0=makeQuery(id+"F52.opPattern","COPY",BODY,{"derivedFrom":makeQuery(id+"F51.opPattern","COPY",BODY,{"derivedFrom":makeQuery(id+"F50.opPattern","COPY",BODY,{"derivedFrom":makeQuery(id+"F49.opPattern","COPY",BODY,{"derivedFrom":makeQuery(id+"F48.opPattern","COPY",BODY,{"derivedFrom":makeQuery(id+"F47.opPattern","COPY",BODY,{"derivedFrom":makeQuery(id+"F35.opExtrude","SWEPT_BODY",BODY,{"disambiguationData":[OSD([sQuery(id+"F34.wireOp",EDGE,"E17.bottom"),sQuery(id+"F34.wireOp",EDGE,"E17.top"),sQuery(id+"F34.wireOp",EDGE,"E17.left"),sQuery(id+"F34.wireOp",EDGE,"E17.right")])]}),"instanceName":"1"}),"instanceName":"1"}),"instanceName":"1"}),"instanceName":"1"}),"instanceName":"1"}),"instanceName":"1"});
            deleteBodies(context, id + "F54", {"entities" : qUnion([Q0])});
        }
        {
            var Q0;
            Q0=makeQuery(id+"F53.opPattern","COPY",BODY,{"derivedFrom":makeQuery(id+"F51.opPattern","COPY",BODY,{"derivedFrom":makeQuery(id+"F50.opPattern","COPY",BODY,{"derivedFrom":makeQuery(id+"F49.opPattern","COPY",BODY,{"derivedFrom":makeQuery(id+"F48.opPattern","COPY",BODY,{"derivedFrom":makeQuery(id+"F47.opPattern","COPY",BODY,{"derivedFrom":makeQuery(id+"F35.opExtrude","SWEPT_BODY",BODY,{"disambiguationData":[OSD([sQuery(id+"F34.wireOp",EDGE,"E17.bottom"),sQuery(id+"F34.wireOp",EDGE,"E17.top"),sQuery(id+"F34.wireOp",EDGE,"E17.left"),sQuery(id+"F34.wireOp",EDGE,"E17.right")])]}),"instanceName":"1"}),"instanceName":"1"}),"instanceName":"1"}),"instanceName":"1"}),"instanceName":"1"}),"instanceName":"1"});
            transform(context, id + "F55", {"entities" : qUnion([Q0]), "transformType" : TransformType.TRANSLATION_3D, "dx" : 0 * mm, "dy" : 50.8 * mm, "dz" : 0 * mm, "makeCopy" : true});
        }
        {
            var Q0;
            Q0=makeQuery(id+"F50.opPattern","COPY",BODY,{"derivedFrom":makeQuery(id+"F49.opPattern","COPY",BODY,{"derivedFrom":makeQuery(id+"F48.opPattern","COPY",BODY,{"derivedFrom":makeQuery(id+"F47.opPattern","COPY",BODY,{"derivedFrom":makeQuery(id+"F35.opExtrude","SWEPT_BODY",BODY,{"disambiguationData":[OSD([sQuery(id+"F34.wireOp",EDGE,"E17.bottom"),sQuery(id+"F34.wireOp",EDGE,"E17.top"),sQuery(id+"F34.wireOp",EDGE,"E17.left"),sQuery(id+"F34.wireOp",EDGE,"E17.right")])]}),"instanceName":"1"}),"instanceName":"1"}),"instanceName":"1"}),"instanceName":"1"});
            var Q1;
            Q1=makeQuery(id+"F4.opExtrude","SWEPT_BODY",BODY,{"disambiguationData":[OSD([sQuery(id+"F1.wireOp",EDGE,"E1.bottom"),sQuery(id+"F1.wireOp",EDGE,"E1.top"),sQuery(id+"F1.wireOp",EDGE,"E1.left"),sQuery(id+"F1.wireOp",EDGE,"E1.right")])]});
            transform(context, id + "F56", {"entities" : qUnion([Q0, Q1]), "transformType" : TransformType.TRANSLATION_3D, "dx" : 0 * mm, "dy" : 50.8 * mm, "dz" : 0 * mm, "makeCopy" : true});
        }
        {
            var Q0;
            Q0=makeQuery(id+"F56.opPattern","COPY",BODY,{"derivedFrom":makeQuery(id+"F4.opExtrude","SWEPT_BODY",BODY,{"disambiguationData":[OSD([sQuery(id+"F1.wireOp",EDGE,"E1.bottom"),sQuery(id+"F1.wireOp",EDGE,"E1.top"),sQuery(id+"F1.wireOp",EDGE,"E1.left"),sQuery(id+"F1.wireOp",EDGE,"E1.right")])]}),"instanceName":"1"});
            deleteBodies(context, id + "F57", {"entities" : qUnion([Q0])});
        }
        {
            var Q0;
            Q0=makeQuery(id+"F46.opPattern","COPY",BODY,{"derivedFrom":makeQuery(id+"F45.opPattern","COPY",BODY,{"derivedFrom":makeQuery(id+"F44.opPattern","COPY",BODY,{"derivedFrom":makeQuery(id+"F31.opExtrude","SWEPT_BODY",BODY,{"disambiguationData":[OSD([sQuery(id+"F30.wireOp",EDGE,"E15.bottom"),sQuery(id+"F30.wireOp",EDGE,"E15.top"),sQuery(id+"F30.wireOp",EDGE,"E15.left"),sQuery(id+"F30.wireOp",EDGE,"E15.right")])]}),"instanceName":"1"}),"instanceName":"1"}),"instanceName":"1"});
            transform(context, id + "F58", {"entities" : qUnion([Q0]), "transformType" : TransformType.TRANSLATION_3D, "dx" : 0 * mm, "dy" : -50.8 * mm, "dz" : 0 * mm, "makeCopy" : true});
        }
        {
            var Q0;
            Q0=makeQuery(id+"F58.opPattern","COPY",BODY,{"derivedFrom":makeQuery(id+"F46.opPattern","COPY",BODY,{"derivedFrom":makeQuery(id+"F45.opPattern","COPY",BODY,{"derivedFrom":makeQuery(id+"F44.opPattern","COPY",BODY,{"derivedFrom":makeQuery(id+"F31.opExtrude","SWEPT_BODY",BODY,{"disambiguationData":[OSD([sQuery(id+"F30.wireOp",EDGE,"E15.bottom"),sQuery(id+"F30.wireOp",EDGE,"E15.top"),sQuery(id+"F30.wireOp",EDGE,"E15.left"),sQuery(id+"F30.wireOp",EDGE,"E15.right")])]}),"instanceName":"1"}),"instanceName":"1"}),"instanceName":"1"}),"instanceName":"1"});
            transform(context, id + "F59", {"entities" : qUnion([Q0]), "transformType" : TransformType.TRANSLATION_3D, "dx" : 0 * mm, "dy" : -50.8 * mm, "dz" : 0 * mm, "makeCopy" : true});
        }
        {
            var Q0;
            Q0=makeQuery(id+"F59.opPattern","COPY",BODY,{"derivedFrom":makeQuery(id+"F58.opPattern","COPY",BODY,{"derivedFrom":makeQuery(id+"F46.opPattern","COPY",BODY,{"derivedFrom":makeQuery(id+"F45.opPattern","COPY",BODY,{"derivedFrom":makeQuery(id+"F44.opPattern","COPY",BODY,{"derivedFrom":makeQuery(id+"F31.opExtrude","SWEPT_BODY",BODY,{"disambiguationData":[OSD([sQuery(id+"F30.wireOp",EDGE,"E15.bottom"),sQuery(id+"F30.wireOp",EDGE,"E15.top"),sQuery(id+"F30.wireOp",EDGE,"E15.left"),sQuery(id+"F30.wireOp",EDGE,"E15.right")])]}),"instanceName":"1"}),"instanceName":"1"}),"instanceName":"1"}),"instanceName":"1"}),"instanceName":"1"});
            transform(context, id + "F60", {"entities" : qUnion([Q0]), "transformType" : TransformType.TRANSLATION_3D, "dx" : 0 * mm, "dy" : -50.8 * mm, "dz" : 0 * mm, "makeCopy" : true});
        }
        {
            var Q0;
            Q0=makeQuery(id+"F58.opPattern","COPY",BODY,{"derivedFrom":makeQuery(id+"F46.opPattern","COPY",BODY,{"derivedFrom":makeQuery(id+"F45.opPattern","COPY",BODY,{"derivedFrom":makeQuery(id+"F44.opPattern","COPY",BODY,{"derivedFrom":makeQuery(id+"F31.opExtrude","SWEPT_BODY",BODY,{"disambiguationData":[OSD([sQuery(id+"F30.wireOp",EDGE,"E15.bottom"),sQuery(id+"F30.wireOp",EDGE,"E15.top"),sQuery(id+"F30.wireOp",EDGE,"E15.left"),sQuery(id+"F30.wireOp",EDGE,"E15.right")])]}),"instanceName":"1"}),"instanceName":"1"}),"instanceName":"1"}),"instanceName":"1"});
            var Q1;
            Q1=makeQuery(id+"F44.opPattern","COPY",BODY,{"derivedFrom":makeQuery(id+"F31.opExtrude","SWEPT_BODY",BODY,{"disambiguationData":[OSD([sQuery(id+"F30.wireOp",EDGE,"E15.bottom"),sQuery(id+"F30.wireOp",EDGE,"E15.top"),sQuery(id+"F30.wireOp",EDGE,"E15.left"),sQuery(id+"F30.wireOp",EDGE,"E15.right")])]}),"instanceName":"1"});
            transform(context, id + "F61", {"entities" : qUnion([Q0, Q1]), "transformType" : TransformType.TRANSLATION_3D, "dx" : 101.6 * mm, "dy" : 0 * mm, "dz" : 0 * mm, "makeCopy" : true});
        }
        {
            var Q0;
            Q0=makeQuery(id+"F61.opPattern","COPY",BODY,{"derivedFrom":makeQuery(id+"F58.opPattern","COPY",BODY,{"derivedFrom":makeQuery(id+"F46.opPattern","COPY",BODY,{"derivedFrom":makeQuery(id+"F45.opPattern","COPY",BODY,{"derivedFrom":makeQuery(id+"F44.opPattern","COPY",BODY,{"derivedFrom":makeQuery(id+"F31.opExtrude","SWEPT_BODY",BODY,{"disambiguationData":[OSD([sQuery(id+"F30.wireOp",EDGE,"E15.bottom"),sQuery(id+"F30.wireOp",EDGE,"E15.top"),sQuery(id+"F30.wireOp",EDGE,"E15.left"),sQuery(id+"F30.wireOp",EDGE,"E15.right")])]}),"instanceName":"1"}),"instanceName":"1"}),"instanceName":"1"}),"instanceName":"1"}),"instanceName":"1"});
            transform(context, id + "F62", {"entities" : qUnion([Q0]), "transformType" : TransformType.TRANSLATION_3D, "dx" : 0 * mm, "dy" : 50.8 * mm, "dz" : 0 * mm, "makeCopy" : true});
        }
        {
            var Q0;
            Q0=makeQuery(id+"F62.opPattern","COPY",BODY,{"derivedFrom":makeQuery(id+"F61.opPattern","COPY",BODY,{"derivedFrom":makeQuery(id+"F58.opPattern","COPY",BODY,{"derivedFrom":makeQuery(id+"F46.opPattern","COPY",BODY,{"derivedFrom":makeQuery(id+"F45.opPattern","COPY",BODY,{"derivedFrom":makeQuery(id+"F44.opPattern","COPY",BODY,{"derivedFrom":makeQuery(id+"F31.opExtrude","SWEPT_BODY",BODY,{"disambiguationData":[OSD([sQuery(id+"F30.wireOp",EDGE,"E15.bottom"),sQuery(id+"F30.wireOp",EDGE,"E15.top"),sQuery(id+"F30.wireOp",EDGE,"E15.left"),sQuery(id+"F30.wireOp",EDGE,"E15.right")])]}),"instanceName":"1"}),"instanceName":"1"}),"instanceName":"1"}),"instanceName":"1"}),"instanceName":"1"}),"instanceName":"1"});
            transform(context, id + "F63", {"entities" : qUnion([Q0]), "transformType" : TransformType.TRANSLATION_3D, "dx" : -50.8 * mm, "dy" : 0 * mm, "dz" : 0 * mm, "makeCopy" : true});
        }
        {
            var Q0;
            Q0=makeQuery(id+"F62.opPattern","COPY",BODY,{"derivedFrom":makeQuery(id+"F61.opPattern","COPY",BODY,{"derivedFrom":makeQuery(id+"F58.opPattern","COPY",BODY,{"derivedFrom":makeQuery(id+"F46.opPattern","COPY",BODY,{"derivedFrom":makeQuery(id+"F45.opPattern","COPY",BODY,{"derivedFrom":makeQuery(id+"F44.opPattern","COPY",BODY,{"derivedFrom":makeQuery(id+"F31.opExtrude","SWEPT_BODY",BODY,{"disambiguationData":[OSD([sQuery(id+"F30.wireOp",EDGE,"E15.bottom"),sQuery(id+"F30.wireOp",EDGE,"E15.top"),sQuery(id+"F30.wireOp",EDGE,"E15.left"),sQuery(id+"F30.wireOp",EDGE,"E15.right")])]}),"instanceName":"1"}),"instanceName":"1"}),"instanceName":"1"}),"instanceName":"1"}),"instanceName":"1"}),"instanceName":"1"});
            transform(context, id + "F64", {"entities" : qUnion([Q0]), "transformType" : TransformType.TRANSLATION_3D, "dx" : 50.8 * mm, "dy" : 0 * mm, "dz" : 0 * mm, "makeCopy" : true});
        }
        {
            var Q0;
            Q0=makeQuery(id+"F63.opPattern","COPY",BODY,{"derivedFrom":makeQuery(id+"F62.opPattern","COPY",BODY,{"derivedFrom":makeQuery(id+"F61.opPattern","COPY",BODY,{"derivedFrom":makeQuery(id+"F58.opPattern","COPY",BODY,{"derivedFrom":makeQuery(id+"F46.opPattern","COPY",BODY,{"derivedFrom":makeQuery(id+"F45.opPattern","COPY",BODY,{"derivedFrom":makeQuery(id+"F44.opPattern","COPY",BODY,{"derivedFrom":makeQuery(id+"F31.opExtrude","SWEPT_BODY",BODY,{"disambiguationData":[OSD([sQuery(id+"F30.wireOp",EDGE,"E15.bottom"),sQuery(id+"F30.wireOp",EDGE,"E15.top"),sQuery(id+"F30.wireOp",EDGE,"E15.left"),sQuery(id+"F30.wireOp",EDGE,"E15.right")])]}),"instanceName":"1"}),"instanceName":"1"}),"instanceName":"1"}),"instanceName":"1"}),"instanceName":"1"}),"instanceName":"1"}),"instanceName":"1"});
            transform(context, id + "F65", {"entities" : qUnion([Q0]), "transformType" : TransformType.TRANSLATION_3D, "dx" : 25.4 * mm, "dy" : -25.4 * mm, "dz" : 0 * mm, "makeCopy" : true});
        }
        {
            var Q0;
            Q0=makeQuery(id+"F65.opPattern","COPY",BODY,{"derivedFrom":makeQuery(id+"F63.opPattern","COPY",BODY,{"derivedFrom":makeQuery(id+"F62.opPattern","COPY",BODY,{"derivedFrom":makeQuery(id+"F61.opPattern","COPY",BODY,{"derivedFrom":makeQuery(id+"F58.opPattern","COPY",BODY,{"derivedFrom":makeQuery(id+"F46.opPattern","COPY",BODY,{"derivedFrom":makeQuery(id+"F45.opPattern","COPY",BODY,{"derivedFrom":makeQuery(id+"F44.opPattern","COPY",BODY,{"derivedFrom":makeQuery(id+"F31.opExtrude","SWEPT_BODY",BODY,{"disambiguationData":[OSD([sQuery(id+"F30.wireOp",EDGE,"E15.bottom"),sQuery(id+"F30.wireOp",EDGE,"E15.top"),sQuery(id+"F30.wireOp",EDGE,"E15.left"),sQuery(id+"F30.wireOp",EDGE,"E15.right")])]}),"instanceName":"1"}),"instanceName":"1"}),"instanceName":"1"}),"instanceName":"1"}),"instanceName":"1"}),"instanceName":"1"}),"instanceName":"1"}),"instanceName":"1"});
            transform(context, id + "F66", {"entities" : qUnion([Q0]), "transformType" : TransformType.TRANSLATION_3D, "dx" : 50.8 * mm, "dy" : 0 * mm, "dz" : 0 * mm, "makeCopy" : true});
        }
        {
            var Q0;
            Q0=makeQuery(id+"F66.opPattern","COPY",BODY,{"derivedFrom":makeQuery(id+"F65.opPattern","COPY",BODY,{"derivedFrom":makeQuery(id+"F63.opPattern","COPY",BODY,{"derivedFrom":makeQuery(id+"F62.opPattern","COPY",BODY,{"derivedFrom":makeQuery(id+"F61.opPattern","COPY",BODY,{"derivedFrom":makeQuery(id+"F58.opPattern","COPY",BODY,{"derivedFrom":makeQuery(id+"F46.opPattern","COPY",BODY,{"derivedFrom":makeQuery(id+"F45.opPattern","COPY",BODY,{"derivedFrom":makeQuery(id+"F44.opPattern","COPY",BODY,{"derivedFrom":makeQuery(id+"F31.opExtrude","SWEPT_BODY",BODY,{"disambiguationData":[OSD([sQuery(id+"F30.wireOp",EDGE,"E15.bottom"),sQuery(id+"F30.wireOp",EDGE,"E15.top"),sQuery(id+"F30.wireOp",EDGE,"E15.left"),sQuery(id+"F30.wireOp",EDGE,"E15.right")])]}),"instanceName":"1"}),"instanceName":"1"}),"instanceName":"1"}),"instanceName":"1"}),"instanceName":"1"}),"instanceName":"1"}),"instanceName":"1"}),"instanceName":"1"}),"instanceName":"1"});
            transform(context, id + "F67", {"entities" : qUnion([Q0]), "transformType" : TransformType.TRANSLATION_3D, "dx" : 50.8 * mm, "dy" : 0 * mm, "dz" : 0 * mm, "makeCopy" : true});
        }
        {
            var Q0;
            Q0=makeQuery(id+"F67.opPattern","COPY",BODY,{"derivedFrom":makeQuery(id+"F66.opPattern","COPY",BODY,{"derivedFrom":makeQuery(id+"F65.opPattern","COPY",BODY,{"derivedFrom":makeQuery(id+"F63.opPattern","COPY",BODY,{"derivedFrom":makeQuery(id+"F62.opPattern","COPY",BODY,{"derivedFrom":makeQuery(id+"F61.opPattern","COPY",BODY,{"derivedFrom":makeQuery(id+"F58.opPattern","COPY",BODY,{"derivedFrom":makeQuery(id+"F46.opPattern","COPY",BODY,{"derivedFrom":makeQuery(id+"F45.opPattern","COPY",BODY,{"derivedFrom":makeQuery(id+"F44.opPattern","COPY",BODY,{"derivedFrom":makeQuery(id+"F31.opExtrude","SWEPT_BODY",BODY,{"disambiguationData":[OSD([sQuery(id+"F30.wireOp",EDGE,"E15.bottom"),sQuery(id+"F30.wireOp",EDGE,"E15.top"),sQuery(id+"F30.wireOp",EDGE,"E15.left"),sQuery(id+"F30.wireOp",EDGE,"E15.right")])]}),"instanceName":"1"}),"instanceName":"1"}),"instanceName":"1"}),"instanceName":"1"}),"instanceName":"1"}),"instanceName":"1"}),"instanceName":"1"}),"instanceName":"1"}),"instanceName":"1"}),"instanceName":"1"});
            transform(context, id + "F68", {"entities" : qUnion([Q0]), "transformType" : TransformType.TRANSLATION_3D, "dx" : 0 * mm, "dy" : -50.8 * mm, "dz" : 0 * mm, "makeCopy" : true});
        }
        {
            var Q0;
            Q0=makeQuery(id+"F68.opPattern","COPY",BODY,{"derivedFrom":makeQuery(id+"F67.opPattern","COPY",BODY,{"derivedFrom":makeQuery(id+"F66.opPattern","COPY",BODY,{"derivedFrom":makeQuery(id+"F65.opPattern","COPY",BODY,{"derivedFrom":makeQuery(id+"F63.opPattern","COPY",BODY,{"derivedFrom":makeQuery(id+"F62.opPattern","COPY",BODY,{"derivedFrom":makeQuery(id+"F61.opPattern","COPY",BODY,{"derivedFrom":makeQuery(id+"F58.opPattern","COPY",BODY,{"derivedFrom":makeQuery(id+"F46.opPattern","COPY",BODY,{"derivedFrom":makeQuery(id+"F45.opPattern","COPY",BODY,{"derivedFrom":makeQuery(id+"F44.opPattern","COPY",BODY,{"derivedFrom":makeQuery(id+"F31.opExtrude","SWEPT_BODY",BODY,{"disambiguationData":[OSD([sQuery(id+"F30.wireOp",EDGE,"E15.bottom"),sQuery(id+"F30.wireOp",EDGE,"E15.top"),sQuery(id+"F30.wireOp",EDGE,"E15.left"),sQuery(id+"F30.wireOp",EDGE,"E15.right")])]}),"instanceName":"1"}),"instanceName":"1"}),"instanceName":"1"}),"instanceName":"1"}),"instanceName":"1"}),"instanceName":"1"}),"instanceName":"1"}),"instanceName":"1"}),"instanceName":"1"}),"instanceName":"1"}),"instanceName":"1"});
            transform(context, id + "F69", {"entities" : qUnion([Q0]), "transformType" : TransformType.TRANSLATION_3D, "dx" : 0 * mm, "dy" : -50.8 * mm, "dz" : 0 * mm, "makeCopy" : true});
        }
        {
            var Q0;
            Q0=makeQuery(id+"F69.opPattern","COPY",BODY,{"derivedFrom":makeQuery(id+"F68.opPattern","COPY",BODY,{"derivedFrom":makeQuery(id+"F67.opPattern","COPY",BODY,{"derivedFrom":makeQuery(id+"F66.opPattern","COPY",BODY,{"derivedFrom":makeQuery(id+"F65.opPattern","COPY",BODY,{"derivedFrom":makeQuery(id+"F63.opPattern","COPY",BODY,{"derivedFrom":makeQuery(id+"F62.opPattern","COPY",BODY,{"derivedFrom":makeQuery(id+"F61.opPattern","COPY",BODY,{"derivedFrom":makeQuery(id+"F58.opPattern","COPY",BODY,{"derivedFrom":makeQuery(id+"F46.opPattern","COPY",BODY,{"derivedFrom":makeQuery(id+"F45.opPattern","COPY",BODY,{"derivedFrom":makeQuery(id+"F44.opPattern","COPY",BODY,{"derivedFrom":makeQuery(id+"F31.opExtrude","SWEPT_BODY",BODY,{"disambiguationData":[OSD([sQuery(id+"F30.wireOp",EDGE,"E15.bottom"),sQuery(id+"F30.wireOp",EDGE,"E15.top"),sQuery(id+"F30.wireOp",EDGE,"E15.left"),sQuery(id+"F30.wireOp",EDGE,"E15.right")])]}),"instanceName":"1"}),"instanceName":"1"}),"instanceName":"1"}),"instanceName":"1"}),"instanceName":"1"}),"instanceName":"1"}),"instanceName":"1"}),"instanceName":"1"}),"instanceName":"1"}),"instanceName":"1"}),"instanceName":"1"}),"instanceName":"1"});
            transform(context, id + "F70", {"entities" : qUnion([Q0]), "transformType" : TransformType.TRANSLATION_3D, "dx" : -25.4 * mm, "dy" : 25.4 * mm, "dz" : 0 * mm, "makeCopy" : true});
        }
        {
            var Q0;
            Q0=makeQuery(id+"F70.opPattern","COPY",BODY,{"derivedFrom":makeQuery(id+"F69.opPattern","COPY",BODY,{"derivedFrom":makeQuery(id+"F68.opPattern","COPY",BODY,{"derivedFrom":makeQuery(id+"F67.opPattern","COPY",BODY,{"derivedFrom":makeQuery(id+"F66.opPattern","COPY",BODY,{"derivedFrom":makeQuery(id+"F65.opPattern","COPY",BODY,{"derivedFrom":makeQuery(id+"F63.opPattern","COPY",BODY,{"derivedFrom":makeQuery(id+"F62.opPattern","COPY",BODY,{"derivedFrom":makeQuery(id+"F61.opPattern","COPY",BODY,{"derivedFrom":makeQuery(id+"F58.opPattern","COPY",BODY,{"derivedFrom":makeQuery(id+"F46.opPattern","COPY",BODY,{"derivedFrom":makeQuery(id+"F45.opPattern","COPY",BODY,{"derivedFrom":makeQuery(id+"F44.opPattern","COPY",BODY,{"derivedFrom":makeQuery(id+"F31.opExtrude","SWEPT_BODY",BODY,{"disambiguationData":[OSD([sQuery(id+"F30.wireOp",EDGE,"E15.bottom"),sQuery(id+"F30.wireOp",EDGE,"E15.top"),sQuery(id+"F30.wireOp",EDGE,"E15.left"),sQuery(id+"F30.wireOp",EDGE,"E15.right")])]}),"instanceName":"1"}),"instanceName":"1"}),"instanceName":"1"}),"instanceName":"1"}),"instanceName":"1"}),"instanceName":"1"}),"instanceName":"1"}),"instanceName":"1"}),"instanceName":"1"}),"instanceName":"1"}),"instanceName":"1"}),"instanceName":"1"}),"instanceName":"1"});
            transform(context, id + "F71", {"entities" : qUnion([Q0]), "transformType" : TransformType.TRANSLATION_3D, "dx" : -25.4 * mm, "dy" : 25.4 * mm, "dz" : 0 * mm, "makeCopy" : true});
        }
        {
            var Q0;
            Q0=makeQuery(id+"F69.opPattern","COPY",BODY,{"derivedFrom":makeQuery(id+"F68.opPattern","COPY",BODY,{"derivedFrom":makeQuery(id+"F67.opPattern","COPY",BODY,{"derivedFrom":makeQuery(id+"F66.opPattern","COPY",BODY,{"derivedFrom":makeQuery(id+"F65.opPattern","COPY",BODY,{"derivedFrom":makeQuery(id+"F63.opPattern","COPY",BODY,{"derivedFrom":makeQuery(id+"F62.opPattern","COPY",BODY,{"derivedFrom":makeQuery(id+"F61.opPattern","COPY",BODY,{"derivedFrom":makeQuery(id+"F58.opPattern","COPY",BODY,{"derivedFrom":makeQuery(id+"F46.opPattern","COPY",BODY,{"derivedFrom":makeQuery(id+"F45.opPattern","COPY",BODY,{"derivedFrom":makeQuery(id+"F44.opPattern","COPY",BODY,{"derivedFrom":makeQuery(id+"F31.opExtrude","SWEPT_BODY",BODY,{"disambiguationData":[OSD([sQuery(id+"F30.wireOp",EDGE,"E15.bottom"),sQuery(id+"F30.wireOp",EDGE,"E15.top"),sQuery(id+"F30.wireOp",EDGE,"E15.left"),sQuery(id+"F30.wireOp",EDGE,"E15.right")])]}),"instanceName":"1"}),"instanceName":"1"}),"instanceName":"1"}),"instanceName":"1"}),"instanceName":"1"}),"instanceName":"1"}),"instanceName":"1"}),"instanceName":"1"}),"instanceName":"1"}),"instanceName":"1"}),"instanceName":"1"}),"instanceName":"1"});
            transform(context, id + "F72", {"entities" : qUnion([Q0]), "transformType" : TransformType.TRANSLATION_3D, "dx" : -76.2 * mm, "dy" : -25.4 * mm, "dz" : 0 * mm, "makeCopy" : true});
        }
        {
            var Q0;
            Q0=makeQuery(id+"F72.opPattern","COPY",BODY,{"derivedFrom":makeQuery(id+"F69.opPattern","COPY",BODY,{"derivedFrom":makeQuery(id+"F68.opPattern","COPY",BODY,{"derivedFrom":makeQuery(id+"F67.opPattern","COPY",BODY,{"derivedFrom":makeQuery(id+"F66.opPattern","COPY",BODY,{"derivedFrom":makeQuery(id+"F65.opPattern","COPY",BODY,{"derivedFrom":makeQuery(id+"F63.opPattern","COPY",BODY,{"derivedFrom":makeQuery(id+"F62.opPattern","COPY",BODY,{"derivedFrom":makeQuery(id+"F61.opPattern","COPY",BODY,{"derivedFrom":makeQuery(id+"F58.opPattern","COPY",BODY,{"derivedFrom":makeQuery(id+"F46.opPattern","COPY",BODY,{"derivedFrom":makeQuery(id+"F45.opPattern","COPY",BODY,{"derivedFrom":makeQuery(id+"F44.opPattern","COPY",BODY,{"derivedFrom":makeQuery(id+"F31.opExtrude","SWEPT_BODY",BODY,{"disambiguationData":[OSD([sQuery(id+"F30.wireOp",EDGE,"E15.bottom"),sQuery(id+"F30.wireOp",EDGE,"E15.top"),sQuery(id+"F30.wireOp",EDGE,"E15.left"),sQuery(id+"F30.wireOp",EDGE,"E15.right")])]}),"instanceName":"1"}),"instanceName":"1"}),"instanceName":"1"}),"instanceName":"1"}),"instanceName":"1"}),"instanceName":"1"}),"instanceName":"1"}),"instanceName":"1"}),"instanceName":"1"}),"instanceName":"1"}),"instanceName":"1"}),"instanceName":"1"}),"instanceName":"1"});
            transform(context, id + "F73", {"entities" : qUnion([Q0]), "transformType" : TransformType.TRANSLATION_3D, "dx" : -50.8 * mm, "dy" : 0 * mm, "dz" : 0 * mm, "makeCopy" : true});
        }
        {
            var Q0;
            Q0=makeQuery(id+"F40.opPattern","COPY",BODY,{"derivedFrom":makeQuery(id+"F39.opPattern","COPY",BODY,{"derivedFrom":makeQuery(id+"F38.opPattern","COPY",BODY,{"derivedFrom":makeQuery(id+"F37.opExtrude","SWEPT_BODY",BODY,{"disambiguationData":[OSD([sQuery(id+"F36.wireOp",EDGE,"E18.bottom"),sQuery(id+"F36.wireOp",EDGE,"E18.top"),sQuery(id+"F36.wireOp",EDGE,"E18.left"),sQuery(id+"F36.wireOp",EDGE,"E18.right")])]}),"instanceName":"1"}),"instanceName":"1"}),"instanceName":"1"});
            transform(context, id + "F74", {"entities" : qUnion([Q0]), "transformType" : TransformType.TRANSLATION_3D, "dx" : 0 * mm, "dy" : -50.8 * mm, "dz" : 0 * mm, "makeCopy" : true});
        }
        {
            var Q0;
            Q0=makeQuery(id+"F74.opPattern","COPY",BODY,{"derivedFrom":makeQuery(id+"F40.opPattern","COPY",BODY,{"derivedFrom":makeQuery(id+"F39.opPattern","COPY",BODY,{"derivedFrom":makeQuery(id+"F38.opPattern","COPY",BODY,{"derivedFrom":makeQuery(id+"F37.opExtrude","SWEPT_BODY",BODY,{"disambiguationData":[OSD([sQuery(id+"F36.wireOp",EDGE,"E18.bottom"),sQuery(id+"F36.wireOp",EDGE,"E18.top"),sQuery(id+"F36.wireOp",EDGE,"E18.left"),sQuery(id+"F36.wireOp",EDGE,"E18.right")])]}),"instanceName":"1"}),"instanceName":"1"}),"instanceName":"1"}),"instanceName":"1"});
            transform(context, id + "F75", {"entities" : qUnion([Q0]), "transformType" : TransformType.TRANSLATION_3D, "dx" : 0 * mm, "dy" : -50.8 * mm, "dz" : 0 * mm, "makeCopy" : true});
        }
        {
            var Q0;
            Q0=makeQuery(id+"F75.opPattern","COPY",BODY,{"derivedFrom":makeQuery(id+"F74.opPattern","COPY",BODY,{"derivedFrom":makeQuery(id+"F40.opPattern","COPY",BODY,{"derivedFrom":makeQuery(id+"F39.opPattern","COPY",BODY,{"derivedFrom":makeQuery(id+"F38.opPattern","COPY",BODY,{"derivedFrom":makeQuery(id+"F37.opExtrude","SWEPT_BODY",BODY,{"disambiguationData":[OSD([sQuery(id+"F36.wireOp",EDGE,"E18.bottom"),sQuery(id+"F36.wireOp",EDGE,"E18.top"),sQuery(id+"F36.wireOp",EDGE,"E18.left"),sQuery(id+"F36.wireOp",EDGE,"E18.right")])]}),"instanceName":"1"}),"instanceName":"1"}),"instanceName":"1"}),"instanceName":"1"}),"instanceName":"1"});
            transform(context, id + "F76", {"entities" : qUnion([Q0]), "transformType" : TransformType.TRANSLATION_3D, "dx" : 0 * mm, "dy" : -50.8 * mm, "dz" : 0 * mm, "makeCopy" : true});
        }
        {
            var Q0;
            Q0=makeQuery(id+"F76.opPattern","COPY",BODY,{"derivedFrom":makeQuery(id+"F75.opPattern","COPY",BODY,{"derivedFrom":makeQuery(id+"F74.opPattern","COPY",BODY,{"derivedFrom":makeQuery(id+"F40.opPattern","COPY",BODY,{"derivedFrom":makeQuery(id+"F39.opPattern","COPY",BODY,{"derivedFrom":makeQuery(id+"F38.opPattern","COPY",BODY,{"derivedFrom":makeQuery(id+"F37.opExtrude","SWEPT_BODY",BODY,{"disambiguationData":[OSD([sQuery(id+"F36.wireOp",EDGE,"E18.bottom"),sQuery(id+"F36.wireOp",EDGE,"E18.top"),sQuery(id+"F36.wireOp",EDGE,"E18.left"),sQuery(id+"F36.wireOp",EDGE,"E18.right")])]}),"instanceName":"1"}),"instanceName":"1"}),"instanceName":"1"}),"instanceName":"1"}),"instanceName":"1"}),"instanceName":"1"});
            transform(context, id + "F77", {"entities" : qUnion([Q0]), "transformType" : TransformType.TRANSLATION_3D, "dx" : -25.4 * mm, "dy" : -25.4 * mm, "dz" : 0 * mm, "makeCopy" : true});
        }
        {
            var Q0;
            Q0=makeQuery(id+"F77.opPattern","COPY",BODY,{"derivedFrom":makeQuery(id+"F76.opPattern","COPY",BODY,{"derivedFrom":makeQuery(id+"F75.opPattern","COPY",BODY,{"derivedFrom":makeQuery(id+"F74.opPattern","COPY",BODY,{"derivedFrom":makeQuery(id+"F40.opPattern","COPY",BODY,{"derivedFrom":makeQuery(id+"F39.opPattern","COPY",BODY,{"derivedFrom":makeQuery(id+"F38.opPattern","COPY",BODY,{"derivedFrom":makeQuery(id+"F37.opExtrude","SWEPT_BODY",BODY,{"disambiguationData":[OSD([sQuery(id+"F36.wireOp",EDGE,"E18.bottom"),sQuery(id+"F36.wireOp",EDGE,"E18.top"),sQuery(id+"F36.wireOp",EDGE,"E18.left"),sQuery(id+"F36.wireOp",EDGE,"E18.right")])]}),"instanceName":"1"}),"instanceName":"1"}),"instanceName":"1"}),"instanceName":"1"}),"instanceName":"1"}),"instanceName":"1"}),"instanceName":"1"});
            transform(context, id + "F78", {"entities" : qUnion([Q0]), "transformType" : TransformType.TRANSLATION_3D, "dx" : 0 * mm, "dy" : 50.8 * mm, "dz" : 0 * mm, "makeCopy" : true});
        }
        {
            var Q0;
            Q0=makeQuery(id+"F78.opPattern","COPY",BODY,{"derivedFrom":makeQuery(id+"F77.opPattern","COPY",BODY,{"derivedFrom":makeQuery(id+"F76.opPattern","COPY",BODY,{"derivedFrom":makeQuery(id+"F75.opPattern","COPY",BODY,{"derivedFrom":makeQuery(id+"F74.opPattern","COPY",BODY,{"derivedFrom":makeQuery(id+"F40.opPattern","COPY",BODY,{"derivedFrom":makeQuery(id+"F39.opPattern","COPY",BODY,{"derivedFrom":makeQuery(id+"F38.opPattern","COPY",BODY,{"derivedFrom":makeQuery(id+"F37.opExtrude","SWEPT_BODY",BODY,{"disambiguationData":[OSD([sQuery(id+"F36.wireOp",EDGE,"E18.bottom"),sQuery(id+"F36.wireOp",EDGE,"E18.top"),sQuery(id+"F36.wireOp",EDGE,"E18.left"),sQuery(id+"F36.wireOp",EDGE,"E18.right")])]}),"instanceName":"1"}),"instanceName":"1"}),"instanceName":"1"}),"instanceName":"1"}),"instanceName":"1"}),"instanceName":"1"}),"instanceName":"1"}),"instanceName":"1"});
            transform(context, id + "F79", {"entities" : qUnion([Q0]), "transformType" : TransformType.TRANSLATION_3D, "dx" : 0 * mm, "dy" : 50.8 * mm, "dz" : 0 * mm, "makeCopy" : true});
        }
        {
            var Q0;
            Q0=makeQuery(id+"F77.opPattern","COPY",BODY,{"derivedFrom":makeQuery(id+"F76.opPattern","COPY",BODY,{"derivedFrom":makeQuery(id+"F75.opPattern","COPY",BODY,{"derivedFrom":makeQuery(id+"F74.opPattern","COPY",BODY,{"derivedFrom":makeQuery(id+"F40.opPattern","COPY",BODY,{"derivedFrom":makeQuery(id+"F39.opPattern","COPY",BODY,{"derivedFrom":makeQuery(id+"F38.opPattern","COPY",BODY,{"derivedFrom":makeQuery(id+"F37.opExtrude","SWEPT_BODY",BODY,{"disambiguationData":[OSD([sQuery(id+"F36.wireOp",EDGE,"E18.bottom"),sQuery(id+"F36.wireOp",EDGE,"E18.top"),sQuery(id+"F36.wireOp",EDGE,"E18.left"),sQuery(id+"F36.wireOp",EDGE,"E18.right")])]}),"instanceName":"1"}),"instanceName":"1"}),"instanceName":"1"}),"instanceName":"1"}),"instanceName":"1"}),"instanceName":"1"}),"instanceName":"1"});
            transform(context, id + "F80", {"entities" : qUnion([Q0]), "transformType" : TransformType.TRANSLATION_3D, "dx" : -25.4 * mm, "dy" : 25.4 * mm, "dz" : 0 * mm, "makeCopy" : true});
        }
        {
            var Q0;
            Q0=makeQuery(id+"F80.opPattern","COPY",BODY,{"derivedFrom":makeQuery(id+"F77.opPattern","COPY",BODY,{"derivedFrom":makeQuery(id+"F76.opPattern","COPY",BODY,{"derivedFrom":makeQuery(id+"F75.opPattern","COPY",BODY,{"derivedFrom":makeQuery(id+"F74.opPattern","COPY",BODY,{"derivedFrom":makeQuery(id+"F40.opPattern","COPY",BODY,{"derivedFrom":makeQuery(id+"F39.opPattern","COPY",BODY,{"derivedFrom":makeQuery(id+"F38.opPattern","COPY",BODY,{"derivedFrom":makeQuery(id+"F37.opExtrude","SWEPT_BODY",BODY,{"disambiguationData":[OSD([sQuery(id+"F36.wireOp",EDGE,"E18.bottom"),sQuery(id+"F36.wireOp",EDGE,"E18.top"),sQuery(id+"F36.wireOp",EDGE,"E18.left"),sQuery(id+"F36.wireOp",EDGE,"E18.right")])]}),"instanceName":"1"}),"instanceName":"1"}),"instanceName":"1"}),"instanceName":"1"}),"instanceName":"1"}),"instanceName":"1"}),"instanceName":"1"}),"instanceName":"1"});
            transform(context, id + "F81", {"entities" : qUnion([Q0]), "transformType" : TransformType.TRANSLATION_3D, "dx" : 0 * mm, "dy" : 50.8 * mm, "dz" : 0 * mm, "makeCopy" : true});
        }
        {
            var Q0;
            Q0=makeQuery(id+"F81.opPattern","COPY",BODY,{"derivedFrom":makeQuery(id+"F80.opPattern","COPY",BODY,{"derivedFrom":makeQuery(id+"F77.opPattern","COPY",BODY,{"derivedFrom":makeQuery(id+"F76.opPattern","COPY",BODY,{"derivedFrom":makeQuery(id+"F75.opPattern","COPY",BODY,{"derivedFrom":makeQuery(id+"F74.opPattern","COPY",BODY,{"derivedFrom":makeQuery(id+"F40.opPattern","COPY",BODY,{"derivedFrom":makeQuery(id+"F39.opPattern","COPY",BODY,{"derivedFrom":makeQuery(id+"F38.opPattern","COPY",BODY,{"derivedFrom":makeQuery(id+"F37.opExtrude","SWEPT_BODY",BODY,{"disambiguationData":[OSD([sQuery(id+"F36.wireOp",EDGE,"E18.bottom"),sQuery(id+"F36.wireOp",EDGE,"E18.top"),sQuery(id+"F36.wireOp",EDGE,"E18.left"),sQuery(id+"F36.wireOp",EDGE,"E18.right")])]}),"instanceName":"1"}),"instanceName":"1"}),"instanceName":"1"}),"instanceName":"1"}),"instanceName":"1"}),"instanceName":"1"}),"instanceName":"1"}),"instanceName":"1"}),"instanceName":"1"});
            transform(context, id + "F82", {"entities" : qUnion([Q0]), "transformType" : TransformType.TRANSLATION_3D, "dx" : 0 * mm, "dy" : 101.6 * mm, "dz" : 0 * mm, "makeCopy" : true});
        }
        {
            var Q0;
            Q0=makeQuery(id+"F82.opPattern","COPY",BODY,{"derivedFrom":makeQuery(id+"F81.opPattern","COPY",BODY,{"derivedFrom":makeQuery(id+"F80.opPattern","COPY",BODY,{"derivedFrom":makeQuery(id+"F77.opPattern","COPY",BODY,{"derivedFrom":makeQuery(id+"F76.opPattern","COPY",BODY,{"derivedFrom":makeQuery(id+"F75.opPattern","COPY",BODY,{"derivedFrom":makeQuery(id+"F74.opPattern","COPY",BODY,{"derivedFrom":makeQuery(id+"F40.opPattern","COPY",BODY,{"derivedFrom":makeQuery(id+"F39.opPattern","COPY",BODY,{"derivedFrom":makeQuery(id+"F38.opPattern","COPY",BODY,{"derivedFrom":makeQuery(id+"F37.opExtrude","SWEPT_BODY",BODY,{"disambiguationData":[OSD([sQuery(id+"F36.wireOp",EDGE,"E18.bottom"),sQuery(id+"F36.wireOp",EDGE,"E18.top"),sQuery(id+"F36.wireOp",EDGE,"E18.left"),sQuery(id+"F36.wireOp",EDGE,"E18.right")])]}),"instanceName":"1"}),"instanceName":"1"}),"instanceName":"1"}),"instanceName":"1"}),"instanceName":"1"}),"instanceName":"1"}),"instanceName":"1"}),"instanceName":"1"}),"instanceName":"1"}),"instanceName":"1"});
            transform(context, id + "F83", {"entities" : qUnion([Q0]), "transformType" : TransformType.TRANSLATION_3D, "dx" : -25.4 * mm, "dy" : -25.4 * mm, "dz" : 0 * mm, "makeCopy" : true});
        }
        {
            var Q0;
            Q0=makeQuery(id+"F83.opPattern","COPY",BODY,{"derivedFrom":makeQuery(id+"F82.opPattern","COPY",BODY,{"derivedFrom":makeQuery(id+"F81.opPattern","COPY",BODY,{"derivedFrom":makeQuery(id+"F80.opPattern","COPY",BODY,{"derivedFrom":makeQuery(id+"F77.opPattern","COPY",BODY,{"derivedFrom":makeQuery(id+"F76.opPattern","COPY",BODY,{"derivedFrom":makeQuery(id+"F75.opPattern","COPY",BODY,{"derivedFrom":makeQuery(id+"F74.opPattern","COPY",BODY,{"derivedFrom":makeQuery(id+"F40.opPattern","COPY",BODY,{"derivedFrom":makeQuery(id+"F39.opPattern","COPY",BODY,{"derivedFrom":makeQuery(id+"F38.opPattern","COPY",BODY,{"derivedFrom":makeQuery(id+"F37.opExtrude","SWEPT_BODY",BODY,{"disambiguationData":[OSD([sQuery(id+"F36.wireOp",EDGE,"E18.bottom"),sQuery(id+"F36.wireOp",EDGE,"E18.top"),sQuery(id+"F36.wireOp",EDGE,"E18.left"),sQuery(id+"F36.wireOp",EDGE,"E18.right")])]}),"instanceName":"1"}),"instanceName":"1"}),"instanceName":"1"}),"instanceName":"1"}),"instanceName":"1"}),"instanceName":"1"}),"instanceName":"1"}),"instanceName":"1"}),"instanceName":"1"}),"instanceName":"1"}),"instanceName":"1"});
            transform(context, id + "F84", {"entities" : qUnion([Q0]), "transformType" : TransformType.TRANSLATION_3D, "dx" : 0 * mm, "dy" : -101.6 * mm, "dz" : 0 * mm, "makeCopy" : true});
        }
        {
            var Q0;
            Q0=makeQuery(id+"F84.opPattern","COPY",BODY,{"derivedFrom":makeQuery(id+"F83.opPattern","COPY",BODY,{"derivedFrom":makeQuery(id+"F82.opPattern","COPY",BODY,{"derivedFrom":makeQuery(id+"F81.opPattern","COPY",BODY,{"derivedFrom":makeQuery(id+"F80.opPattern","COPY",BODY,{"derivedFrom":makeQuery(id+"F77.opPattern","COPY",BODY,{"derivedFrom":makeQuery(id+"F76.opPattern","COPY",BODY,{"derivedFrom":makeQuery(id+"F75.opPattern","COPY",BODY,{"derivedFrom":makeQuery(id+"F74.opPattern","COPY",BODY,{"derivedFrom":makeQuery(id+"F40.opPattern","COPY",BODY,{"derivedFrom":makeQuery(id+"F39.opPattern","COPY",BODY,{"derivedFrom":makeQuery(id+"F38.opPattern","COPY",BODY,{"derivedFrom":makeQuery(id+"F37.opExtrude","SWEPT_BODY",BODY,{"disambiguationData":[OSD([sQuery(id+"F36.wireOp",EDGE,"E18.bottom"),sQuery(id+"F36.wireOp",EDGE,"E18.top"),sQuery(id+"F36.wireOp",EDGE,"E18.left"),sQuery(id+"F36.wireOp",EDGE,"E18.right")])]}),"instanceName":"1"}),"instanceName":"1"}),"instanceName":"1"}),"instanceName":"1"}),"instanceName":"1"}),"instanceName":"1"}),"instanceName":"1"}),"instanceName":"1"}),"instanceName":"1"}),"instanceName":"1"}),"instanceName":"1"}),"instanceName":"1"});
            transform(context, id + "F85", {"entities" : qUnion([Q0]), "transformType" : TransformType.TRANSLATION_3D, "dx" : 0 * mm, "dy" : -50.8 * mm, "dz" : 0 * mm, "makeCopy" : true});
        }
        {
            var Q0;
            Q0=makeQuery(id+"F85.opPattern","COPY",BODY,{"derivedFrom":makeQuery(id+"F84.opPattern","COPY",BODY,{"derivedFrom":makeQuery(id+"F83.opPattern","COPY",BODY,{"derivedFrom":makeQuery(id+"F82.opPattern","COPY",BODY,{"derivedFrom":makeQuery(id+"F81.opPattern","COPY",BODY,{"derivedFrom":makeQuery(id+"F80.opPattern","COPY",BODY,{"derivedFrom":makeQuery(id+"F77.opPattern","COPY",BODY,{"derivedFrom":makeQuery(id+"F76.opPattern","COPY",BODY,{"derivedFrom":makeQuery(id+"F75.opPattern","COPY",BODY,{"derivedFrom":makeQuery(id+"F74.opPattern","COPY",BODY,{"derivedFrom":makeQuery(id+"F40.opPattern","COPY",BODY,{"derivedFrom":makeQuery(id+"F39.opPattern","COPY",BODY,{"derivedFrom":makeQuery(id+"F38.opPattern","COPY",BODY,{"derivedFrom":makeQuery(id+"F37.opExtrude","SWEPT_BODY",BODY,{"disambiguationData":[OSD([sQuery(id+"F36.wireOp",EDGE,"E18.bottom"),sQuery(id+"F36.wireOp",EDGE,"E18.top"),sQuery(id+"F36.wireOp",EDGE,"E18.left"),sQuery(id+"F36.wireOp",EDGE,"E18.right")])]}),"instanceName":"1"}),"instanceName":"1"}),"instanceName":"1"}),"instanceName":"1"}),"instanceName":"1"}),"instanceName":"1"}),"instanceName":"1"}),"instanceName":"1"}),"instanceName":"1"}),"instanceName":"1"}),"instanceName":"1"}),"instanceName":"1"}),"instanceName":"1"});
            transform(context, id + "F86", {"entities" : qUnion([Q0]), "transformType" : TransformType.TRANSLATION_3D, "dx" : -25.4 * mm, "dy" : 25.4 * mm, "dz" : 0 * mm, "makeCopy" : true});
        }
        {
            var Q0;
            Q0=makeQuery(id+"F86.opPattern","COPY",BODY,{"derivedFrom":makeQuery(id+"F85.opPattern","COPY",BODY,{"derivedFrom":makeQuery(id+"F84.opPattern","COPY",BODY,{"derivedFrom":makeQuery(id+"F83.opPattern","COPY",BODY,{"derivedFrom":makeQuery(id+"F82.opPattern","COPY",BODY,{"derivedFrom":makeQuery(id+"F81.opPattern","COPY",BODY,{"derivedFrom":makeQuery(id+"F80.opPattern","COPY",BODY,{"derivedFrom":makeQuery(id+"F77.opPattern","COPY",BODY,{"derivedFrom":makeQuery(id+"F76.opPattern","COPY",BODY,{"derivedFrom":makeQuery(id+"F75.opPattern","COPY",BODY,{"derivedFrom":makeQuery(id+"F74.opPattern","COPY",BODY,{"derivedFrom":makeQuery(id+"F40.opPattern","COPY",BODY,{"derivedFrom":makeQuery(id+"F39.opPattern","COPY",BODY,{"derivedFrom":makeQuery(id+"F38.opPattern","COPY",BODY,{"derivedFrom":makeQuery(id+"F37.opExtrude","SWEPT_BODY",BODY,{"disambiguationData":[OSD([sQuery(id+"F36.wireOp",EDGE,"E18.bottom"),sQuery(id+"F36.wireOp",EDGE,"E18.top"),sQuery(id+"F36.wireOp",EDGE,"E18.left"),sQuery(id+"F36.wireOp",EDGE,"E18.right")])]}),"instanceName":"1"}),"instanceName":"1"}),"instanceName":"1"}),"instanceName":"1"}),"instanceName":"1"}),"instanceName":"1"}),"instanceName":"1"}),"instanceName":"1"}),"instanceName":"1"}),"instanceName":"1"}),"instanceName":"1"}),"instanceName":"1"}),"instanceName":"1"}),"instanceName":"1"});
            transform(context, id + "F87", {"entities" : qUnion([Q0]), "transformType" : TransformType.TRANSLATION_3D, "dx" : 0 * mm, "dy" : 101.6 * mm, "dz" : 0 * mm, "makeCopy" : true});
        }
        {
            var Q0;
            Q0=makeQuery(id+"F87.opPattern","COPY",BODY,{"derivedFrom":makeQuery(id+"F86.opPattern","COPY",BODY,{"derivedFrom":makeQuery(id+"F85.opPattern","COPY",BODY,{"derivedFrom":makeQuery(id+"F84.opPattern","COPY",BODY,{"derivedFrom":makeQuery(id+"F83.opPattern","COPY",BODY,{"derivedFrom":makeQuery(id+"F82.opPattern","COPY",BODY,{"derivedFrom":makeQuery(id+"F81.opPattern","COPY",BODY,{"derivedFrom":makeQuery(id+"F80.opPattern","COPY",BODY,{"derivedFrom":makeQuery(id+"F77.opPattern","COPY",BODY,{"derivedFrom":makeQuery(id+"F76.opPattern","COPY",BODY,{"derivedFrom":makeQuery(id+"F75.opPattern","COPY",BODY,{"derivedFrom":makeQuery(id+"F74.opPattern","COPY",BODY,{"derivedFrom":makeQuery(id+"F40.opPattern","COPY",BODY,{"derivedFrom":makeQuery(id+"F39.opPattern","COPY",BODY,{"derivedFrom":makeQuery(id+"F38.opPattern","COPY",BODY,{"derivedFrom":makeQuery(id+"F37.opExtrude","SWEPT_BODY",BODY,{"disambiguationData":[OSD([sQuery(id+"F36.wireOp",EDGE,"E18.bottom"),sQuery(id+"F36.wireOp",EDGE,"E18.top"),sQuery(id+"F36.wireOp",EDGE,"E18.left"),sQuery(id+"F36.wireOp",EDGE,"E18.right")])]}),"instanceName":"1"}),"instanceName":"1"}),"instanceName":"1"}),"instanceName":"1"}),"instanceName":"1"}),"instanceName":"1"}),"instanceName":"1"}),"instanceName":"1"}),"instanceName":"1"}),"instanceName":"1"}),"instanceName":"1"}),"instanceName":"1"}),"instanceName":"1"}),"instanceName":"1"}),"instanceName":"1"});
            transform(context, id + "F88", {"entities" : qUnion([Q0]), "transformType" : TransformType.TRANSLATION_3D, "dx" : 0 * mm, "dy" : 50.8 * mm, "dz" : 0 * mm, "makeCopy" : true});
        }
        {
            var Q0;
            Q0=makeQuery(id+"F88.opPattern","COPY",BODY,{"derivedFrom":makeQuery(id+"F87.opPattern","COPY",BODY,{"derivedFrom":makeQuery(id+"F86.opPattern","COPY",BODY,{"derivedFrom":makeQuery(id+"F85.opPattern","COPY",BODY,{"derivedFrom":makeQuery(id+"F84.opPattern","COPY",BODY,{"derivedFrom":makeQuery(id+"F83.opPattern","COPY",BODY,{"derivedFrom":makeQuery(id+"F82.opPattern","COPY",BODY,{"derivedFrom":makeQuery(id+"F81.opPattern","COPY",BODY,{"derivedFrom":makeQuery(id+"F80.opPattern","COPY",BODY,{"derivedFrom":makeQuery(id+"F77.opPattern","COPY",BODY,{"derivedFrom":makeQuery(id+"F76.opPattern","COPY",BODY,{"derivedFrom":makeQuery(id+"F75.opPattern","COPY",BODY,{"derivedFrom":makeQuery(id+"F74.opPattern","COPY",BODY,{"derivedFrom":makeQuery(id+"F40.opPattern","COPY",BODY,{"derivedFrom":makeQuery(id+"F39.opPattern","COPY",BODY,{"derivedFrom":makeQuery(id+"F38.opPattern","COPY",BODY,{"derivedFrom":makeQuery(id+"F37.opExtrude","SWEPT_BODY",BODY,{"disambiguationData":[OSD([sQuery(id+"F36.wireOp",EDGE,"E18.bottom"),sQuery(id+"F36.wireOp",EDGE,"E18.top"),sQuery(id+"F36.wireOp",EDGE,"E18.left"),sQuery(id+"F36.wireOp",EDGE,"E18.right")])]}),"instanceName":"1"}),"instanceName":"1"}),"instanceName":"1"}),"instanceName":"1"}),"instanceName":"1"}),"instanceName":"1"}),"instanceName":"1"}),"instanceName":"1"}),"instanceName":"1"}),"instanceName":"1"}),"instanceName":"1"}),"instanceName":"1"}),"instanceName":"1"}),"instanceName":"1"}),"instanceName":"1"}),"instanceName":"1"});
            transform(context, id + "F89", {"entities" : qUnion([Q0]), "transformType" : TransformType.TRANSLATION_3D, "dx" : -25.4 * mm, "dy" : -25.4 * mm, "dz" : 0 * mm, "makeCopy" : true});
        }
        {
            var Q0;
            Q0=makeQuery(id+"F89.opPattern","COPY",BODY,{"derivedFrom":makeQuery(id+"F88.opPattern","COPY",BODY,{"derivedFrom":makeQuery(id+"F87.opPattern","COPY",BODY,{"derivedFrom":makeQuery(id+"F86.opPattern","COPY",BODY,{"derivedFrom":makeQuery(id+"F85.opPattern","COPY",BODY,{"derivedFrom":makeQuery(id+"F84.opPattern","COPY",BODY,{"derivedFrom":makeQuery(id+"F83.opPattern","COPY",BODY,{"derivedFrom":makeQuery(id+"F82.opPattern","COPY",BODY,{"derivedFrom":makeQuery(id+"F81.opPattern","COPY",BODY,{"derivedFrom":makeQuery(id+"F80.opPattern","COPY",BODY,{"derivedFrom":makeQuery(id+"F77.opPattern","COPY",BODY,{"derivedFrom":makeQuery(id+"F76.opPattern","COPY",BODY,{"derivedFrom":makeQuery(id+"F75.opPattern","COPY",BODY,{"derivedFrom":makeQuery(id+"F74.opPattern","COPY",BODY,{"derivedFrom":makeQuery(id+"F40.opPattern","COPY",BODY,{"derivedFrom":makeQuery(id+"F39.opPattern","COPY",BODY,{"derivedFrom":makeQuery(id+"F38.opPattern","COPY",BODY,{"derivedFrom":makeQuery(id+"F37.opExtrude","SWEPT_BODY",BODY,{"disambiguationData":[OSD([sQuery(id+"F36.wireOp",EDGE,"E18.bottom"),sQuery(id+"F36.wireOp",EDGE,"E18.top"),sQuery(id+"F36.wireOp",EDGE,"E18.left"),sQuery(id+"F36.wireOp",EDGE,"E18.right")])]}),"instanceName":"1"}),"instanceName":"1"}),"instanceName":"1"}),"instanceName":"1"}),"instanceName":"1"}),"instanceName":"1"}),"instanceName":"1"}),"instanceName":"1"}),"instanceName":"1"}),"instanceName":"1"}),"instanceName":"1"}),"instanceName":"1"}),"instanceName":"1"}),"instanceName":"1"}),"instanceName":"1"}),"instanceName":"1"}),"instanceName":"1"});
            transform(context, id + "F90", {"entities" : qUnion([Q0]), "transformType" : TransformType.TRANSLATION_3D, "dx" : 0 * mm, "dy" : -50.8 * mm, "dz" : 0 * mm, "makeCopy" : true});
        }
        {
            var Q0;
            Q0=makeQuery(id+"F90.opPattern","COPY",BODY,{"derivedFrom":makeQuery(id+"F89.opPattern","COPY",BODY,{"derivedFrom":makeQuery(id+"F88.opPattern","COPY",BODY,{"derivedFrom":makeQuery(id+"F87.opPattern","COPY",BODY,{"derivedFrom":makeQuery(id+"F86.opPattern","COPY",BODY,{"derivedFrom":makeQuery(id+"F85.opPattern","COPY",BODY,{"derivedFrom":makeQuery(id+"F84.opPattern","COPY",BODY,{"derivedFrom":makeQuery(id+"F83.opPattern","COPY",BODY,{"derivedFrom":makeQuery(id+"F82.opPattern","COPY",BODY,{"derivedFrom":makeQuery(id+"F81.opPattern","COPY",BODY,{"derivedFrom":makeQuery(id+"F80.opPattern","COPY",BODY,{"derivedFrom":makeQuery(id+"F77.opPattern","COPY",BODY,{"derivedFrom":makeQuery(id+"F76.opPattern","COPY",BODY,{"derivedFrom":makeQuery(id+"F75.opPattern","COPY",BODY,{"derivedFrom":makeQuery(id+"F74.opPattern","COPY",BODY,{"derivedFrom":makeQuery(id+"F40.opPattern","COPY",BODY,{"derivedFrom":makeQuery(id+"F39.opPattern","COPY",BODY,{"derivedFrom":makeQuery(id+"F38.opPattern","COPY",BODY,{"derivedFrom":makeQuery(id+"F37.opExtrude","SWEPT_BODY",BODY,{"disambiguationData":[OSD([sQuery(id+"F36.wireOp",EDGE,"E18.bottom"),sQuery(id+"F36.wireOp",EDGE,"E18.top"),sQuery(id+"F36.wireOp",EDGE,"E18.left"),sQuery(id+"F36.wireOp",EDGE,"E18.right")])]}),"instanceName":"1"}),"instanceName":"1"}),"instanceName":"1"}),"instanceName":"1"}),"instanceName":"1"}),"instanceName":"1"}),"instanceName":"1"}),"instanceName":"1"}),"instanceName":"1"}),"instanceName":"1"}),"instanceName":"1"}),"instanceName":"1"}),"instanceName":"1"}),"instanceName":"1"}),"instanceName":"1"}),"instanceName":"1"}),"instanceName":"1"}),"instanceName":"1"});
            transform(context, id + "F91", {"entities" : qUnion([Q0]), "transformType" : TransformType.TRANSLATION_3D, "dx" : 0 * mm, "dy" : -101.6 * mm, "dz" : 0 * mm, "makeCopy" : true});
        }
        {
            var Q0;
            Q0=makeQuery(id+"F91.opPattern","COPY",BODY,{"derivedFrom":makeQuery(id+"F90.opPattern","COPY",BODY,{"derivedFrom":makeQuery(id+"F89.opPattern","COPY",BODY,{"derivedFrom":makeQuery(id+"F88.opPattern","COPY",BODY,{"derivedFrom":makeQuery(id+"F87.opPattern","COPY",BODY,{"derivedFrom":makeQuery(id+"F86.opPattern","COPY",BODY,{"derivedFrom":makeQuery(id+"F85.opPattern","COPY",BODY,{"derivedFrom":makeQuery(id+"F84.opPattern","COPY",BODY,{"derivedFrom":makeQuery(id+"F83.opPattern","COPY",BODY,{"derivedFrom":makeQuery(id+"F82.opPattern","COPY",BODY,{"derivedFrom":makeQuery(id+"F81.opPattern","COPY",BODY,{"derivedFrom":makeQuery(id+"F80.opPattern","COPY",BODY,{"derivedFrom":makeQuery(id+"F77.opPattern","COPY",BODY,{"derivedFrom":makeQuery(id+"F76.opPattern","COPY",BODY,{"derivedFrom":makeQuery(id+"F75.opPattern","COPY",BODY,{"derivedFrom":makeQuery(id+"F74.opPattern","COPY",BODY,{"derivedFrom":makeQuery(id+"F40.opPattern","COPY",BODY,{"derivedFrom":makeQuery(id+"F39.opPattern","COPY",BODY,{"derivedFrom":makeQuery(id+"F38.opPattern","COPY",BODY,{"derivedFrom":makeQuery(id+"F37.opExtrude","SWEPT_BODY",BODY,{"disambiguationData":[OSD([sQuery(id+"F36.wireOp",EDGE,"E18.bottom"),sQuery(id+"F36.wireOp",EDGE,"E18.top"),sQuery(id+"F36.wireOp",EDGE,"E18.left"),sQuery(id+"F36.wireOp",EDGE,"E18.right")])]}),"instanceName":"1"}),"instanceName":"1"}),"instanceName":"1"}),"instanceName":"1"}),"instanceName":"1"}),"instanceName":"1"}),"instanceName":"1"}),"instanceName":"1"}),"instanceName":"1"}),"instanceName":"1"}),"instanceName":"1"}),"instanceName":"1"}),"instanceName":"1"}),"instanceName":"1"}),"instanceName":"1"}),"instanceName":"1"}),"instanceName":"1"}),"instanceName":"1"}),"instanceName":"1"});
            transform(context, id + "F92", {"entities" : qUnion([Q0]), "transformType" : TransformType.TRANSLATION_3D, "dx" : -50.8 * mm, "dy" : 50.8 * mm, "dz" : 0 * mm, "makeCopy" : true});
        }
        {
            var Q0;
            Q0=makeQuery(id+"F92.opPattern","COPY",BODY,{"derivedFrom":makeQuery(id+"F91.opPattern","COPY",BODY,{"derivedFrom":makeQuery(id+"F90.opPattern","COPY",BODY,{"derivedFrom":makeQuery(id+"F89.opPattern","COPY",BODY,{"derivedFrom":makeQuery(id+"F88.opPattern","COPY",BODY,{"derivedFrom":makeQuery(id+"F87.opPattern","COPY",BODY,{"derivedFrom":makeQuery(id+"F86.opPattern","COPY",BODY,{"derivedFrom":makeQuery(id+"F85.opPattern","COPY",BODY,{"derivedFrom":makeQuery(id+"F84.opPattern","COPY",BODY,{"derivedFrom":makeQuery(id+"F83.opPattern","COPY",BODY,{"derivedFrom":makeQuery(id+"F82.opPattern","COPY",BODY,{"derivedFrom":makeQuery(id+"F81.opPattern","COPY",BODY,{"derivedFrom":makeQuery(id+"F80.opPattern","COPY",BODY,{"derivedFrom":makeQuery(id+"F77.opPattern","COPY",BODY,{"derivedFrom":makeQuery(id+"F76.opPattern","COPY",BODY,{"derivedFrom":makeQuery(id+"F75.opPattern","COPY",BODY,{"derivedFrom":makeQuery(id+"F74.opPattern","COPY",BODY,{"derivedFrom":makeQuery(id+"F40.opPattern","COPY",BODY,{"derivedFrom":makeQuery(id+"F39.opPattern","COPY",BODY,{"derivedFrom":makeQuery(id+"F38.opPattern","COPY",BODY,{"derivedFrom":makeQuery(id+"F37.opExtrude","SWEPT_BODY",BODY,{"disambiguationData":[OSD([sQuery(id+"F36.wireOp",EDGE,"E18.bottom"),sQuery(id+"F36.wireOp",EDGE,"E18.top"),sQuery(id+"F36.wireOp",EDGE,"E18.left"),sQuery(id+"F36.wireOp",EDGE,"E18.right")])]}),"instanceName":"1"}),"instanceName":"1"}),"instanceName":"1"}),"instanceName":"1"}),"instanceName":"1"}),"instanceName":"1"}),"instanceName":"1"}),"instanceName":"1"}),"instanceName":"1"}),"instanceName":"1"}),"instanceName":"1"}),"instanceName":"1"}),"instanceName":"1"}),"instanceName":"1"}),"instanceName":"1"}),"instanceName":"1"}),"instanceName":"1"}),"instanceName":"1"}),"instanceName":"1"}),"instanceName":"1"});
            transform(context, id + "F93", {"entities" : qUnion([Q0]), "transformType" : TransformType.TRANSLATION_3D, "dx" : 0 * mm, "dy" : 50.8 * mm, "dz" : 0 * mm, "makeCopy" : true});
        }
        {
            var Q0;
            Q0=makeQuery(id+"F93.opPattern","COPY",BODY,{"derivedFrom":makeQuery(id+"F92.opPattern","COPY",BODY,{"derivedFrom":makeQuery(id+"F91.opPattern","COPY",BODY,{"derivedFrom":makeQuery(id+"F90.opPattern","COPY",BODY,{"derivedFrom":makeQuery(id+"F89.opPattern","COPY",BODY,{"derivedFrom":makeQuery(id+"F88.opPattern","COPY",BODY,{"derivedFrom":makeQuery(id+"F87.opPattern","COPY",BODY,{"derivedFrom":makeQuery(id+"F86.opPattern","COPY",BODY,{"derivedFrom":makeQuery(id+"F85.opPattern","COPY",BODY,{"derivedFrom":makeQuery(id+"F84.opPattern","COPY",BODY,{"derivedFrom":makeQuery(id+"F83.opPattern","COPY",BODY,{"derivedFrom":makeQuery(id+"F82.opPattern","COPY",BODY,{"derivedFrom":makeQuery(id+"F81.opPattern","COPY",BODY,{"derivedFrom":makeQuery(id+"F80.opPattern","COPY",BODY,{"derivedFrom":makeQuery(id+"F77.opPattern","COPY",BODY,{"derivedFrom":makeQuery(id+"F76.opPattern","COPY",BODY,{"derivedFrom":makeQuery(id+"F75.opPattern","COPY",BODY,{"derivedFrom":makeQuery(id+"F74.opPattern","COPY",BODY,{"derivedFrom":makeQuery(id+"F40.opPattern","COPY",BODY,{"derivedFrom":makeQuery(id+"F39.opPattern","COPY",BODY,{"derivedFrom":makeQuery(id+"F38.opPattern","COPY",BODY,{"derivedFrom":makeQuery(id+"F37.opExtrude","SWEPT_BODY",BODY,{"disambiguationData":[OSD([sQuery(id+"F36.wireOp",EDGE,"E18.bottom"),sQuery(id+"F36.wireOp",EDGE,"E18.top"),sQuery(id+"F36.wireOp",EDGE,"E18.left"),sQuery(id+"F36.wireOp",EDGE,"E18.right")])]}),"instanceName":"1"}),"instanceName":"1"}),"instanceName":"1"}),"instanceName":"1"}),"instanceName":"1"}),"instanceName":"1"}),"instanceName":"1"}),"instanceName":"1"}),"instanceName":"1"}),"instanceName":"1"}),"instanceName":"1"}),"instanceName":"1"}),"instanceName":"1"}),"instanceName":"1"}),"instanceName":"1"}),"instanceName":"1"}),"instanceName":"1"}),"instanceName":"1"}),"instanceName":"1"}),"instanceName":"1"}),"instanceName":"1"});
            transform(context, id + "F94", {"entities" : qUnion([Q0]), "transformType" : TransformType.TRANSLATION_3D, "dx" : 0 * mm, "dy" : 50.8 * mm, "dz" : 0 * mm, "makeCopy" : true});
        }
        {
            var Q0;
            Q0=makeQuery(id+"F94.opPattern","COPY",BODY,{"derivedFrom":makeQuery(id+"F93.opPattern","COPY",BODY,{"derivedFrom":makeQuery(id+"F92.opPattern","COPY",BODY,{"derivedFrom":makeQuery(id+"F91.opPattern","COPY",BODY,{"derivedFrom":makeQuery(id+"F90.opPattern","COPY",BODY,{"derivedFrom":makeQuery(id+"F89.opPattern","COPY",BODY,{"derivedFrom":makeQuery(id+"F88.opPattern","COPY",BODY,{"derivedFrom":makeQuery(id+"F87.opPattern","COPY",BODY,{"derivedFrom":makeQuery(id+"F86.opPattern","COPY",BODY,{"derivedFrom":makeQuery(id+"F85.opPattern","COPY",BODY,{"derivedFrom":makeQuery(id+"F84.opPattern","COPY",BODY,{"derivedFrom":makeQuery(id+"F83.opPattern","COPY",BODY,{"derivedFrom":makeQuery(id+"F82.opPattern","COPY",BODY,{"derivedFrom":makeQuery(id+"F81.opPattern","COPY",BODY,{"derivedFrom":makeQuery(id+"F80.opPattern","COPY",BODY,{"derivedFrom":makeQuery(id+"F77.opPattern","COPY",BODY,{"derivedFrom":makeQuery(id+"F76.opPattern","COPY",BODY,{"derivedFrom":makeQuery(id+"F75.opPattern","COPY",BODY,{"derivedFrom":makeQuery(id+"F74.opPattern","COPY",BODY,{"derivedFrom":makeQuery(id+"F40.opPattern","COPY",BODY,{"derivedFrom":makeQuery(id+"F39.opPattern","COPY",BODY,{"derivedFrom":makeQuery(id+"F38.opPattern","COPY",BODY,{"derivedFrom":makeQuery(id+"F37.opExtrude","SWEPT_BODY",BODY,{"disambiguationData":[OSD([sQuery(id+"F36.wireOp",EDGE,"E18.bottom"),sQuery(id+"F36.wireOp",EDGE,"E18.top"),sQuery(id+"F36.wireOp",EDGE,"E18.left"),sQuery(id+"F36.wireOp",EDGE,"E18.right")])]}),"instanceName":"1"}),"instanceName":"1"}),"instanceName":"1"}),"instanceName":"1"}),"instanceName":"1"}),"instanceName":"1"}),"instanceName":"1"}),"instanceName":"1"}),"instanceName":"1"}),"instanceName":"1"}),"instanceName":"1"}),"instanceName":"1"}),"instanceName":"1"}),"instanceName":"1"}),"instanceName":"1"}),"instanceName":"1"}),"instanceName":"1"}),"instanceName":"1"}),"instanceName":"1"}),"instanceName":"1"}),"instanceName":"1"}),"instanceName":"1"});
            transform(context, id + "F95", {"entities" : qUnion([Q0]), "transformType" : TransformType.TRANSLATION_3D, "dx" : 25.4 * mm, "dy" : 25.4 * mm, "dz" : 0 * mm, "makeCopy" : true});
        }
        {
            var Q0;
            Q0=makeQuery(id+"F95.opPattern","COPY",BODY,{"derivedFrom":makeQuery(id+"F94.opPattern","COPY",BODY,{"derivedFrom":makeQuery(id+"F93.opPattern","COPY",BODY,{"derivedFrom":makeQuery(id+"F92.opPattern","COPY",BODY,{"derivedFrom":makeQuery(id+"F91.opPattern","COPY",BODY,{"derivedFrom":makeQuery(id+"F90.opPattern","COPY",BODY,{"derivedFrom":makeQuery(id+"F89.opPattern","COPY",BODY,{"derivedFrom":makeQuery(id+"F88.opPattern","COPY",BODY,{"derivedFrom":makeQuery(id+"F87.opPattern","COPY",BODY,{"derivedFrom":makeQuery(id+"F86.opPattern","COPY",BODY,{"derivedFrom":makeQuery(id+"F85.opPattern","COPY",BODY,{"derivedFrom":makeQuery(id+"F84.opPattern","COPY",BODY,{"derivedFrom":makeQuery(id+"F83.opPattern","COPY",BODY,{"derivedFrom":makeQuery(id+"F82.opPattern","COPY",BODY,{"derivedFrom":makeQuery(id+"F81.opPattern","COPY",BODY,{"derivedFrom":makeQuery(id+"F80.opPattern","COPY",BODY,{"derivedFrom":makeQuery(id+"F77.opPattern","COPY",BODY,{"derivedFrom":makeQuery(id+"F76.opPattern","COPY",BODY,{"derivedFrom":makeQuery(id+"F75.opPattern","COPY",BODY,{"derivedFrom":makeQuery(id+"F74.opPattern","COPY",BODY,{"derivedFrom":makeQuery(id+"F40.opPattern","COPY",BODY,{"derivedFrom":makeQuery(id+"F39.opPattern","COPY",BODY,{"derivedFrom":makeQuery(id+"F38.opPattern","COPY",BODY,{"derivedFrom":makeQuery(id+"F37.opExtrude","SWEPT_BODY",BODY,{"disambiguationData":[OSD([sQuery(id+"F36.wireOp",EDGE,"E18.bottom"),sQuery(id+"F36.wireOp",EDGE,"E18.top"),sQuery(id+"F36.wireOp",EDGE,"E18.left"),sQuery(id+"F36.wireOp",EDGE,"E18.right")])]}),"instanceName":"1"}),"instanceName":"1"}),"instanceName":"1"}),"instanceName":"1"}),"instanceName":"1"}),"instanceName":"1"}),"instanceName":"1"}),"instanceName":"1"}),"instanceName":"1"}),"instanceName":"1"}),"instanceName":"1"}),"instanceName":"1"}),"instanceName":"1"}),"instanceName":"1"}),"instanceName":"1"}),"instanceName":"1"}),"instanceName":"1"}),"instanceName":"1"}),"instanceName":"1"}),"instanceName":"1"}),"instanceName":"1"}),"instanceName":"1"}),"instanceName":"1"});
            transform(context, id + "F96", {"entities" : qUnion([Q0]), "transformType" : TransformType.TRANSLATION_3D, "dx" : 0 * mm, "dy" : -50.8 * mm, "dz" : 0 * mm, "makeCopy" : true});
        }
        {
            var Q0;
            Q0=makeQuery(id+"F96.opPattern","COPY",BODY,{"derivedFrom":makeQuery(id+"F95.opPattern","COPY",BODY,{"derivedFrom":makeQuery(id+"F94.opPattern","COPY",BODY,{"derivedFrom":makeQuery(id+"F93.opPattern","COPY",BODY,{"derivedFrom":makeQuery(id+"F92.opPattern","COPY",BODY,{"derivedFrom":makeQuery(id+"F91.opPattern","COPY",BODY,{"derivedFrom":makeQuery(id+"F90.opPattern","COPY",BODY,{"derivedFrom":makeQuery(id+"F89.opPattern","COPY",BODY,{"derivedFrom":makeQuery(id+"F88.opPattern","COPY",BODY,{"derivedFrom":makeQuery(id+"F87.opPattern","COPY",BODY,{"derivedFrom":makeQuery(id+"F86.opPattern","COPY",BODY,{"derivedFrom":makeQuery(id+"F85.opPattern","COPY",BODY,{"derivedFrom":makeQuery(id+"F84.opPattern","COPY",BODY,{"derivedFrom":makeQuery(id+"F83.opPattern","COPY",BODY,{"derivedFrom":makeQuery(id+"F82.opPattern","COPY",BODY,{"derivedFrom":makeQuery(id+"F81.opPattern","COPY",BODY,{"derivedFrom":makeQuery(id+"F80.opPattern","COPY",BODY,{"derivedFrom":makeQuery(id+"F77.opPattern","COPY",BODY,{"derivedFrom":makeQuery(id+"F76.opPattern","COPY",BODY,{"derivedFrom":makeQuery(id+"F75.opPattern","COPY",BODY,{"derivedFrom":makeQuery(id+"F74.opPattern","COPY",BODY,{"derivedFrom":makeQuery(id+"F40.opPattern","COPY",BODY,{"derivedFrom":makeQuery(id+"F39.opPattern","COPY",BODY,{"derivedFrom":makeQuery(id+"F38.opPattern","COPY",BODY,{"derivedFrom":makeQuery(id+"F37.opExtrude","SWEPT_BODY",BODY,{"disambiguationData":[OSD([sQuery(id+"F36.wireOp",EDGE,"E18.bottom"),sQuery(id+"F36.wireOp",EDGE,"E18.top"),sQuery(id+"F36.wireOp",EDGE,"E18.left"),sQuery(id+"F36.wireOp",EDGE,"E18.right")])]}),"instanceName":"1"}),"instanceName":"1"}),"instanceName":"1"}),"instanceName":"1"}),"instanceName":"1"}),"instanceName":"1"}),"instanceName":"1"}),"instanceName":"1"}),"instanceName":"1"}),"instanceName":"1"}),"instanceName":"1"}),"instanceName":"1"}),"instanceName":"1"}),"instanceName":"1"}),"instanceName":"1"}),"instanceName":"1"}),"instanceName":"1"}),"instanceName":"1"}),"instanceName":"1"}),"instanceName":"1"}),"instanceName":"1"}),"instanceName":"1"}),"instanceName":"1"}),"instanceName":"1"});
            transform(context, id + "F97", {"entities" : qUnion([Q0]), "transformType" : TransformType.TRANSLATION_3D, "dx" : 0 * mm, "dy" : -50.8 * mm, "dz" : 0 * mm, "makeCopy" : true});
        }
        {
            var Q0;
            Q0=makeQuery(id+"F70.opPattern","COPY",BODY,{"derivedFrom":makeQuery(id+"F69.opPattern","COPY",BODY,{"derivedFrom":makeQuery(id+"F68.opPattern","COPY",BODY,{"derivedFrom":makeQuery(id+"F67.opPattern","COPY",BODY,{"derivedFrom":makeQuery(id+"F66.opPattern","COPY",BODY,{"derivedFrom":makeQuery(id+"F65.opPattern","COPY",BODY,{"derivedFrom":makeQuery(id+"F63.opPattern","COPY",BODY,{"derivedFrom":makeQuery(id+"F62.opPattern","COPY",BODY,{"derivedFrom":makeQuery(id+"F61.opPattern","COPY",BODY,{"derivedFrom":makeQuery(id+"F58.opPattern","COPY",BODY,{"derivedFrom":makeQuery(id+"F46.opPattern","COPY",BODY,{"derivedFrom":makeQuery(id+"F45.opPattern","COPY",BODY,{"derivedFrom":makeQuery(id+"F44.opPattern","COPY",BODY,{"derivedFrom":makeQuery(id+"F31.opExtrude","SWEPT_BODY",BODY,{"disambiguationData":[OSD([sQuery(id+"F30.wireOp",EDGE,"E15.bottom"),sQuery(id+"F30.wireOp",EDGE,"E15.top"),sQuery(id+"F30.wireOp",EDGE,"E15.left"),sQuery(id+"F30.wireOp",EDGE,"E15.right")])]}),"instanceName":"1"}),"instanceName":"1"}),"instanceName":"1"}),"instanceName":"1"}),"instanceName":"1"}),"instanceName":"1"}),"instanceName":"1"}),"instanceName":"1"}),"instanceName":"1"}),"instanceName":"1"}),"instanceName":"1"}),"instanceName":"1"}),"instanceName":"1"});
            transform(context, id + "F98", {"entities" : qUnion([Q0]), "transformType" : TransformType.TRANSLATION_3D, "dx" : -101.6 * mm, "dy" : 0 * mm, "dz" : 0 * mm, "makeCopy" : true});
        }
    });
